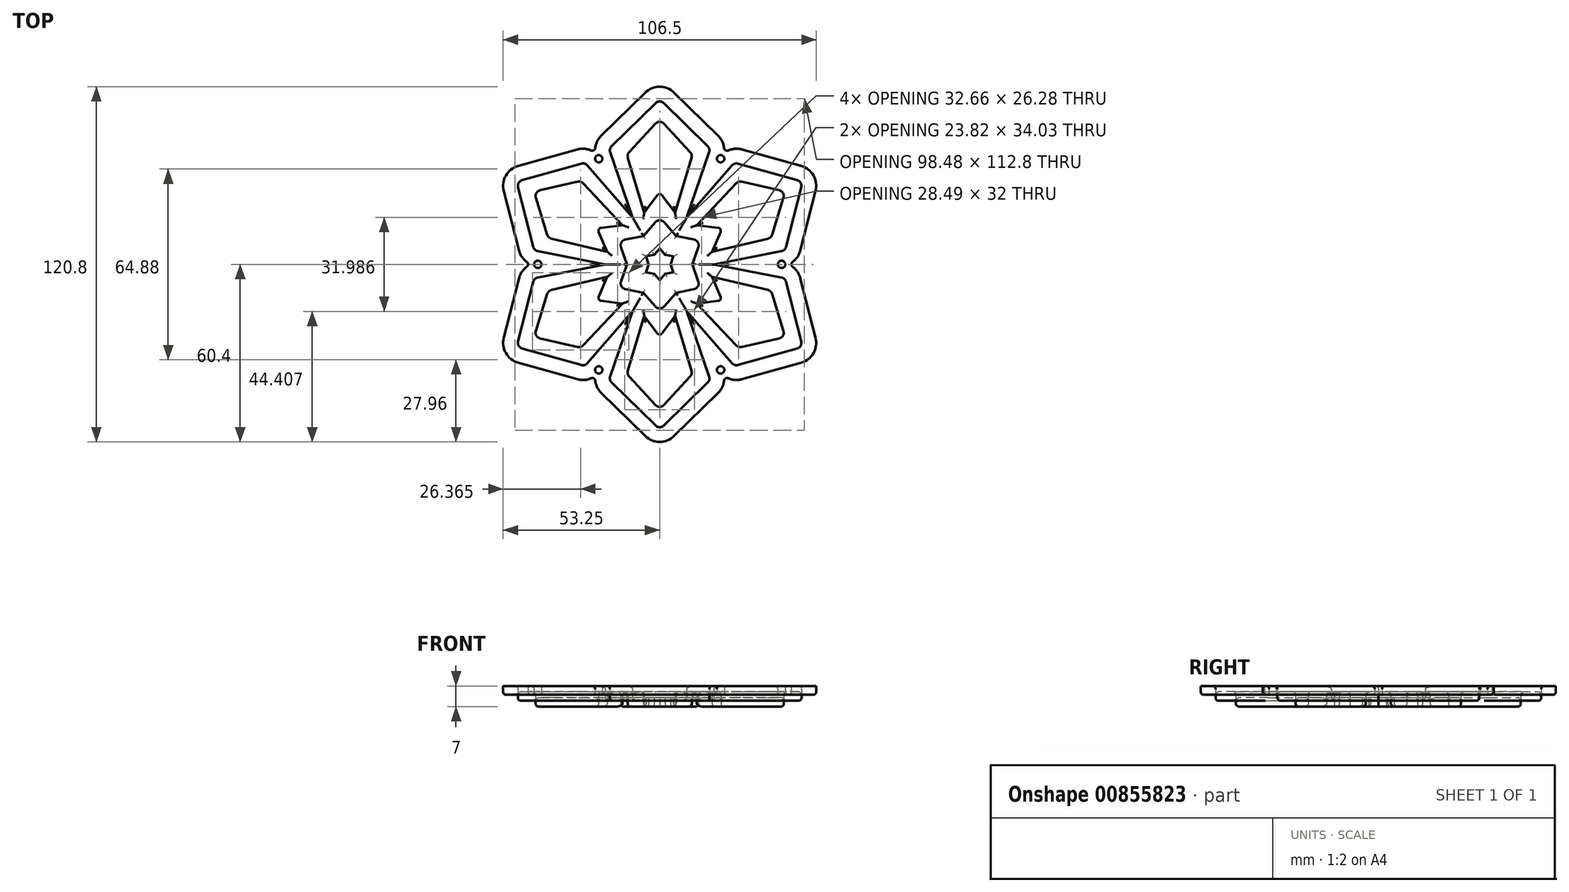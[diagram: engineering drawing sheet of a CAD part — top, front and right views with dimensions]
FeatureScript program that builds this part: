
annotation { "Feature Type Name" : "Feature", "Feature Type Description" : "" }
export const myFeature = defineFeature(function(context is Context, id is Id, definition is map)
    precondition{}
    {
        {
            var Q0;
            Q0=qCreatedBy(makeId("Top.planeOp"),FACE);
            var sketch = newSketch(context, id + "F0", { "sketchPlane" : qUnion([Q0])});
            skLineSegment(sketch, "E0", {"start": v(-3.74, 0) * mm, "end": v(-4.66, 2.7) * mm});
            skLineSegment(sketch, "E1", {"start": v(-16.34, 40.2) * mm, "end": v(-1.4, 54.83) * mm});
            skLineSegment(sketch, "E2.MirrorCS", {"start": v(16.34, 40.2) * mm, "end": v(1.4, 54.83) * mm});
            skLineSegment(sketch, "E3.MirrorCS", {"start": v(3.74, 0) * mm, "end": v(4.66, 2.7) * mm});
            skPoint(sketch, "E4.visualSharp", {"position": v(-17.25, 39.31) * mm});
            skArc(sketch, "E4.filletArc", {"start": v(-16.34, 40.2) * mm, "mid": v(-16.89, 39.23) * mm, "end": v(-16.83, 38.12) * mm});
            skPoint(sketch, "E5.visualSharp", {"position": v(17.25, 39.31) * mm});
            skArc(sketch, "E5.filletArc", {"start": v(16.83, 38.12) * mm, "mid": v(16.89, 39.23) * mm, "end": v(16.34, 40.2) * mm});
            skPoint(sketch, "E6.visualSharp", {"position": v(0, 56.2) * mm});
            skArc(sketch, "E6.filletArc", {"start": v(1.4, 54.83) * mm, "mid": v(0, 55.4) * mm, "end": v(-1.4, 54.83) * mm});
            skPoint(sketch, "E7.1.0", {"position": v(-48.67, 28.1) * mm});
            skPoint(sketch, "E7.1.1", {"position": v(-25.42, 34.6) * mm});
            skLineSegment(sketch, "E7.1.2", {"start": v(1.87, 3.24) * mm, "end": v(0, 5.38) * mm});
            skLineSegment(sketch, "E7.1.3", {"start": v(-26.64, 34.25) * mm, "end": v(-46.78, 28.63) * mm});
            skLineSegment(sketch, "E7.1.4", {"start": v(-42.98, 5.95) * mm, "end": v(-48.18, 26.2) * mm});
            skLineSegment(sketch, "E7.1.5", {"start": v(-1.87, -3.24) * mm, "end": v(-4.66, -2.7) * mm});
            skPoint(sketch, "E7.1.6", {"position": v(-42.67, 4.72) * mm});
            skArc(sketch, "E7.1.7", {"start": v(-46.78, 28.63) * mm, "mid": v(-47.98, 27.7) * mm, "end": v(-48.18, 26.2) * mm});
            skArc(sketch, "E7.1.8", {"start": v(-42.98, 5.95) * mm, "mid": v(-42.42, 4.99) * mm, "end": v(-41.43, 4.48) * mm});
            skArc(sketch, "E7.1.9", {"start": v(-24.6, 33.64) * mm, "mid": v(-25.53, 34.24) * mm, "end": v(-26.64, 34.25) * mm});
            skPoint(sketch, "E7.2.0", {"position": v(-48.67, -28.1) * mm});
            skPoint(sketch, "E7.2.1", {"position": v(-42.67, -4.72) * mm});
            skLineSegment(sketch, "E7.2.2", {"start": v(-1.87, 3.24) * mm, "end": v(-4.66, 2.7) * mm});
            skLineSegment(sketch, "E7.2.3", {"start": v(-42.98, -5.95) * mm, "end": v(-48.18, -26.2) * mm});
            skLineSegment(sketch, "E7.2.4", {"start": v(-26.64, -34.25) * mm, "end": v(-46.78, -28.63) * mm});
            skLineSegment(sketch, "E7.2.5", {"start": v(1.87, -3.24) * mm, "end": v(0, -5.38) * mm});
            skPoint(sketch, "E7.2.6", {"position": v(-25.42, -34.6) * mm});
            skArc(sketch, "E7.2.7", {"start": v(-48.18, -26.2) * mm, "mid": v(-47.98, -27.7) * mm, "end": v(-46.78, -28.63) * mm});
            skArc(sketch, "E7.2.8", {"start": v(-26.64, -34.25) * mm, "mid": v(-25.53, -34.24) * mm, "end": v(-24.6, -33.64) * mm});
            skArc(sketch, "E7.2.9", {"start": v(-41.43, -4.48) * mm, "mid": v(-42.42, -4.99) * mm, "end": v(-42.98, -5.95) * mm});
            skPoint(sketch, "E7.3.0", {"position": v(0, -56.2) * mm});
            skPoint(sketch, "E7.3.1", {"position": v(-17.25, -39.31) * mm});
            skLineSegment(sketch, "E7.3.2", {"start": v(-3.74, 0) * mm, "end": v(-4.66, -2.7) * mm});
            skLineSegment(sketch, "E7.3.3", {"start": v(-16.34, -40.2) * mm, "end": v(-1.4, -54.83) * mm});
            skLineSegment(sketch, "E7.3.4", {"start": v(16.34, -40.2) * mm, "end": v(1.4, -54.83) * mm});
            skLineSegment(sketch, "E7.3.5", {"start": v(3.74, 0) * mm, "end": v(4.66, -2.7) * mm});
            skPoint(sketch, "E7.3.6", {"position": v(17.25, -39.31) * mm});
            skArc(sketch, "E7.3.7", {"start": v(-1.4, -54.83) * mm, "mid": v(0, -55.4) * mm, "end": v(1.4, -54.83) * mm});
            skArc(sketch, "E7.3.8", {"start": v(16.34, -40.2) * mm, "mid": v(16.89, -39.23) * mm, "end": v(16.83, -38.12) * mm});
            skArc(sketch, "E7.3.9", {"start": v(-16.83, -38.12) * mm, "mid": v(-16.89, -39.23) * mm, "end": v(-16.34, -40.2) * mm});
            skPoint(sketch, "E7.4.0", {"position": v(48.67, -28.1) * mm});
            skPoint(sketch, "E7.4.1", {"position": v(25.42, -34.6) * mm});
            skLineSegment(sketch, "E7.4.2", {"start": v(-1.87, -3.24) * mm, "end": v(0, -5.38) * mm});
            skLineSegment(sketch, "E7.4.3", {"start": v(26.64, -34.25) * mm, "end": v(46.78, -28.63) * mm});
            skLineSegment(sketch, "E7.4.4", {"start": v(42.98, -5.95) * mm, "end": v(48.18, -26.2) * mm});
            skLineSegment(sketch, "E7.4.5", {"start": v(1.87, 3.24) * mm, "end": v(4.66, 2.7) * mm});
            skPoint(sketch, "E7.4.6", {"position": v(42.67, -4.72) * mm});
            skArc(sketch, "E7.4.7", {"start": v(46.78, -28.63) * mm, "mid": v(47.98, -27.7) * mm, "end": v(48.18, -26.2) * mm});
            skArc(sketch, "E7.4.8", {"start": v(42.98, -5.95) * mm, "mid": v(42.42, -4.99) * mm, "end": v(41.43, -4.48) * mm});
            skArc(sketch, "E7.4.9", {"start": v(24.6, -33.64) * mm, "mid": v(25.53, -34.24) * mm, "end": v(26.64, -34.25) * mm});
            skPoint(sketch, "E7.5.0", {"position": v(48.67, 28.1) * mm});
            skPoint(sketch, "E7.5.1", {"position": v(42.67, 4.72) * mm});
            skLineSegment(sketch, "E7.5.2", {"start": v(1.87, -3.24) * mm, "end": v(4.66, -2.7) * mm});
            skLineSegment(sketch, "E7.5.3", {"start": v(42.98, 5.95) * mm, "end": v(48.18, 26.2) * mm});
            skLineSegment(sketch, "E7.5.4", {"start": v(26.64, 34.25) * mm, "end": v(46.78, 28.63) * mm});
            skLineSegment(sketch, "E7.5.5", {"start": v(-1.87, 3.24) * mm, "end": v(0, 5.38) * mm});
            skPoint(sketch, "E7.5.6", {"position": v(25.42, 34.6) * mm});
            skArc(sketch, "E7.5.7", {"start": v(48.18, 26.2) * mm, "mid": v(47.98, 27.7) * mm, "end": v(46.78, 28.63) * mm});
            skArc(sketch, "E7.5.8", {"start": v(26.64, 34.25) * mm, "mid": v(25.53, 34.24) * mm, "end": v(24.6, 33.64) * mm});
            skArc(sketch, "E7.5.9", {"start": v(41.43, 4.48) * mm, "mid": v(42.42, 4.99) * mm, "end": v(42.98, 5.95) * mm});
            skPoint(sketch, "E7.center", {"position": v(0, 0) * mm});
            skLineSegment(sketch, "E8.trimOffspring", {"start": v(-9.23, 16) * mm, "end": v(-24.6, 33.64) * mm});
            skLineSegment(sketch, "E9.trimOffspring", {"start": v(-9.23, 16) * mm, "end": v(-16.83, 38.12) * mm});
            skLineSegment(sketch, "E10.trimOffspring", {"start": v(-18.46, 0) * mm, "end": v(-41.43, -4.48) * mm});
            skLineSegment(sketch, "E11.trimOffspring", {"start": v(-18.46, 0) * mm, "end": v(-41.43, 4.48) * mm});
            skLineSegment(sketch, "E12.trimOffspring", {"start": v(-9.23, -16) * mm, "end": v(-16.83, -38.12) * mm});
            skLineSegment(sketch, "E13.trimOffspring", {"start": v(-9.23, -16) * mm, "end": v(-24.6, -33.64) * mm});
            skLineSegment(sketch, "E14.trimOffspring", {"start": v(9.23, -16) * mm, "end": v(24.6, -33.64) * mm});
            skLineSegment(sketch, "E15.trimOffspring", {"start": v(9.23, -16) * mm, "end": v(16.83, -38.12) * mm});
            skLineSegment(sketch, "E16.trimOffspring", {"start": v(18.46, 0) * mm, "end": v(41.43, 4.48) * mm});
            skLineSegment(sketch, "E17.trimOffspring", {"start": v(18.46, 0) * mm, "end": v(41.43, -4.48) * mm});
            skLineSegment(sketch, "E18.trimOffspring", {"start": v(9.23, 16) * mm, "end": v(16.83, 38.12) * mm});
            skLineSegment(sketch, "E19.trimOffspring", {"start": v(9.23, 16) * mm, "end": v(24.6, 33.64) * mm});
            skLineSegment(sketch, "E20.0", {"start": v(-5.57, 9.65) * mm, "end": v(-11.64, 8.46) * mm});
            skLineSegment(sketch, "E20.1", {"start": v(11.14, 0) * mm, "end": v(13.15, -5.85) * mm});
            skLineSegment(sketch, "E20.2", {"start": v(11.14, 0) * mm, "end": v(13.15, 5.85) * mm});
            skLineSegment(sketch, "E20.3", {"start": v(5.57, 9.65) * mm, "end": v(11.64, 8.46) * mm});
            skLineSegment(sketch, "E20.4", {"start": v(5.57, 9.65) * mm, "end": v(1.5, 14.31) * mm});
            skLineSegment(sketch, "E20.5", {"start": v(5.57, -9.65) * mm, "end": v(11.64, -8.46) * mm});
            skLineSegment(sketch, "E20.6", {"start": v(-5.57, 9.65) * mm, "end": v(-1.5, 14.31) * mm});
            skLineSegment(sketch, "E20.7", {"start": v(5.57, -9.65) * mm, "end": v(1.5, -14.31) * mm});
            skLineSegment(sketch, "E20.8", {"start": v(-5.57, -9.65) * mm, "end": v(-1.5, -14.31) * mm});
            skLineSegment(sketch, "E20.9", {"start": v(-5.57, -9.65) * mm, "end": v(-11.64, -8.46) * mm});
            skLineSegment(sketch, "E20.10", {"start": v(-11.14, 0) * mm, "end": v(-13.15, -5.85) * mm});
            skLineSegment(sketch, "E20.11", {"start": v(-11.14, 0) * mm, "end": v(-13.15, 5.85) * mm});
            skLineSegment(sketch, "E21.0", {"start": v(-27.99, 39.07) * mm, "end": v(-48.13, 33.44) * mm});
            skLineSegment(sketch, "E22.0", {"start": v(-47.83, 4.7) * mm, "end": v(-53.03, 24.96) * mm});
            skArc(sketch, "E23.0", {"start": v(-48.13, 33.44) * mm, "mid": v(-52.3, 30.2) * mm, "end": v(-53.03, 24.96) * mm});
            skArc(sketch, "E24.0", {"start": v(-23.3, 38.74) * mm, "mid": v(-25.61, 39.3) * mm, "end": v(-27.99, 39.07) * mm});
            skArc(sketch, "E25.0", {"start": v(-47.83, 4.7) * mm, "mid": v(-46.85, 2.53) * mm, "end": v(-45.2, 0.8) * mm});
            skArc(sketch, "E26.1.1", {"start": v(-27.99, -39.07) * mm, "mid": v(-25.61, -39.3) * mm, "end": v(-23.3, -38.74) * mm});
            skLineSegment(sketch, "E26.1.2", {"start": v(-27.99, -39.07) * mm, "end": v(-48.13, -33.44) * mm});
            skArc(sketch, "E26.1.3", {"start": v(-53.03, -24.96) * mm, "mid": v(-52.3, -30.2) * mm, "end": v(-48.13, -33.44) * mm});
            skLineSegment(sketch, "E26.1.4", {"start": v(-47.83, -4.7) * mm, "end": v(-53.03, -24.96) * mm});
            skArc(sketch, "E26.1.5", {"start": v(-45.2, -0.8) * mm, "mid": v(-46.85, -2.53) * mm, "end": v(-47.83, -4.7) * mm});
            skArc(sketch, "E26.2.1", {"start": v(19.84, -43.77) * mm, "mid": v(21.24, -41.84) * mm, "end": v(21.9, -39.54) * mm});
            skLineSegment(sketch, "E26.2.2", {"start": v(19.84, -43.77) * mm, "end": v(4.9, -58.4) * mm});
            skArc(sketch, "E26.2.3", {"start": v(-4.9, -58.4) * mm, "mid": v(0, -60.4) * mm, "end": v(4.9, -58.4) * mm});
            skLineSegment(sketch, "E26.2.4", {"start": v(-19.84, -43.77) * mm, "end": v(-4.9, -58.4) * mm});
            skArc(sketch, "E26.2.5", {"start": v(-21.9, -39.54) * mm, "mid": v(-21.24, -41.84) * mm, "end": v(-19.84, -43.77) * mm});
            skArc(sketch, "E26.3.1", {"start": v(47.83, -4.7) * mm, "mid": v(46.85, -2.53) * mm, "end": v(45.2, -0.8) * mm});
            skLineSegment(sketch, "E26.3.2", {"start": v(47.83, -4.7) * mm, "end": v(53.03, -24.96) * mm});
            skArc(sketch, "E26.3.3", {"start": v(48.13, -33.44) * mm, "mid": v(52.3, -30.2) * mm, "end": v(53.03, -24.96) * mm});
            skLineSegment(sketch, "E26.3.4", {"start": v(27.99, -39.07) * mm, "end": v(48.13, -33.44) * mm});
            skArc(sketch, "E26.3.5", {"start": v(23.3, -38.74) * mm, "mid": v(25.61, -39.3) * mm, "end": v(27.99, -39.07) * mm});
            skArc(sketch, "E26.4.1", {"start": v(27.99, 39.07) * mm, "mid": v(25.61, 39.3) * mm, "end": v(23.3, 38.74) * mm});
            skLineSegment(sketch, "E26.4.2", {"start": v(27.99, 39.07) * mm, "end": v(48.13, 33.44) * mm});
            skArc(sketch, "E26.4.3", {"start": v(53.03, 24.96) * mm, "mid": v(52.3, 30.2) * mm, "end": v(48.13, 33.44) * mm});
            skLineSegment(sketch, "E26.4.4", {"start": v(47.83, 4.7) * mm, "end": v(53.03, 24.96) * mm});
            skArc(sketch, "E26.4.5", {"start": v(45.2, 0.8) * mm, "mid": v(46.85, 2.53) * mm, "end": v(47.83, 4.7) * mm});
            skArc(sketch, "E26.5.1", {"start": v(-19.84, 43.77) * mm, "mid": v(-21.24, 41.84) * mm, "end": v(-21.9, 39.54) * mm});
            skLineSegment(sketch, "E26.5.2", {"start": v(-19.84, 43.77) * mm, "end": v(-4.9, 58.4) * mm});
            skArc(sketch, "E26.5.3", {"start": v(4.9, 58.4) * mm, "mid": v(0, 60.4) * mm, "end": v(-4.9, 58.4) * mm});
            skLineSegment(sketch, "E26.5.4", {"start": v(19.84, 43.77) * mm, "end": v(4.9, 58.4) * mm});
            skArc(sketch, "E26.5.5", {"start": v(21.9, 39.54) * mm, "mid": v(21.24, 41.84) * mm, "end": v(19.84, 43.77) * mm});
            skPoint(sketch, "E27.orphan", {"position": v(-20.82, 36.92) * mm});
            skPoint(sketch, "E28.orphan", {"position": v(-21.56, 36.5) * mm});
            skPoint(sketch, "E29.orphan", {"position": v(20.82, 36.92) * mm});
            skPoint(sketch, "E30.orphan", {"position": v(21.56, 36.5) * mm});
            skPoint(sketch, "E31.orphan", {"position": v(42.39, 0.43) * mm});
            skPoint(sketch, "E32.orphan", {"position": v(42.39, -0.43) * mm});
            skPoint(sketch, "E33.orphan", {"position": v(21.56, -36.5) * mm});
            skPoint(sketch, "E34.orphan", {"position": v(20.82, -36.92) * mm});
            skPoint(sketch, "E35.orphan", {"position": v(-20.82, -36.92) * mm});
            skPoint(sketch, "E36.orphan", {"position": v(-21.56, -36.5) * mm});
            skPoint(sketch, "E37.orphan", {"position": v(-42.39, 0.43) * mm});
            skPoint(sketch, "E38.orphan", {"position": v(-42.39, -0.43) * mm});
            skLineSegment(sketch, "E39", {"start": v(-0.8, 23.48) * mm, "end": v(-5.22, 17.6) * mm});
            skLineSegment(sketch, "E40", {"start": v(-5.22, 17.6) * mm, "end": v(-10.83, 36.26) * mm});
            skLineSegment(sketch, "E41", {"start": v(-10.38, 38.2) * mm, "end": v(-1.47, 47.81) * mm});
            skLineSegment(sketch, "E42.MirrorCS", {"start": v(10.38, 38.2) * mm, "end": v(1.47, 47.81) * mm});
            skLineSegment(sketch, "E43.MirrorCS", {"start": v(5.22, 17.6) * mm, "end": v(10.83, 36.26) * mm});
            skLineSegment(sketch, "E44.MirrorCS", {"start": v(0.8, 23.48) * mm, "end": v(5.22, 17.6) * mm});
            skPoint(sketch, "E45.visualSharp", {"position": v(0, 49.4) * mm});
            skArc(sketch, "E45.filletArc", {"start": v(1.47, 47.81) * mm, "mid": v(0, 48.45) * mm, "end": v(-1.47, 47.81) * mm});
            skPoint(sketch, "E46.visualSharp", {"position": v(-11.16, 37.35) * mm});
            skArc(sketch, "E46.filletArc", {"start": v(-10.38, 38.2) * mm, "mid": v(-10.86, 37.28) * mm, "end": v(-10.83, 36.26) * mm});
            skPoint(sketch, "E47.visualSharp", {"position": v(11.16, 37.35) * mm});
            skArc(sketch, "E47.filletArc", {"start": v(10.83, 36.26) * mm, "mid": v(10.86, 37.28) * mm, "end": v(10.38, 38.2) * mm});
            skPoint(sketch, "E48.visualSharp", {"position": v(0, 24.54) * mm});
            skArc(sketch, "E48.filletArc", {"start": v(0.8, 23.48) * mm, "mid": v(0, 23.88) * mm, "end": v(-0.8, 23.48) * mm});
            skPoint(sketch, "E49.visualSharp", {"position": v(0, 16.05) * mm});
            skArc(sketch, "E49.filletArc", {"start": v(1.5, 14.31) * mm, "mid": v(0, 15) * mm, "end": v(-1.5, 14.31) * mm});
            skPoint(sketch, "E50.visualSharp", {"position": v(13.9, 8.02) * mm});
            skArc(sketch, "E50.filletArc", {"start": v(13.15, 5.85) * mm, "mid": v(13, 7.5) * mm, "end": v(11.64, 8.46) * mm});
            skPoint(sketch, "E51.visualSharp", {"position": v(13.9, -8.02) * mm});
            skArc(sketch, "E51.filletArc", {"start": v(11.64, -8.46) * mm, "mid": v(13, -7.5) * mm, "end": v(13.15, -5.85) * mm});
            skPoint(sketch, "E52.visualSharp", {"position": v(0, -16.05) * mm});
            skArc(sketch, "E52.filletArc", {"start": v(-1.5, -14.31) * mm, "mid": v(0, -15) * mm, "end": v(1.5, -14.31) * mm});
            skPoint(sketch, "E53.visualSharp", {"position": v(-13.9, -8.02) * mm});
            skArc(sketch, "E53.filletArc", {"start": v(-13.15, -5.85) * mm, "mid": v(-13, -7.5) * mm, "end": v(-11.64, -8.46) * mm});
            skPoint(sketch, "E54.visualSharp", {"position": v(-13.9, 8.02) * mm});
            skArc(sketch, "E54.filletArc", {"start": v(-11.64, 8.46) * mm, "mid": v(-13, 7.5) * mm, "end": v(-13.15, 5.85) * mm});
            skArc(sketch, "E55.1.0", {"start": v(-25.99, 27.5) * mm, "mid": v(-26.86, 28.05) * mm, "end": v(-27.89, 28.09) * mm});
            skLineSegment(sketch, "E55.1.1", {"start": v(-27.89, 28.09) * mm, "end": v(-40.67, 25.18) * mm});
            skArc(sketch, "E55.1.2", {"start": v(-40.67, 25.18) * mm, "mid": v(-41.96, 24.23) * mm, "end": v(-42.14, 22.64) * mm});
            skLineSegment(sketch, "E55.1.3", {"start": v(-38.27, 10.1) * mm, "end": v(-42.14, 22.64) * mm});
            skArc(sketch, "E55.1.4", {"start": v(-38.27, 10.1) * mm, "mid": v(-37.72, 9.24) * mm, "end": v(-36.81, 8.75) * mm});
            skLineSegment(sketch, "E55.1.5", {"start": v(-17.86, 4.28) * mm, "end": v(-36.81, 8.75) * mm});
            skLineSegment(sketch, "E55.1.6", {"start": v(-20.73, 11.05) * mm, "end": v(-17.86, 4.28) * mm});
            skArc(sketch, "E55.1.7", {"start": v(-19.93, 12.43) * mm, "mid": v(-20.68, 11.94) * mm, "end": v(-20.73, 11.05) * mm});
            skLineSegment(sketch, "E55.1.8", {"start": v(-19.93, 12.43) * mm, "end": v(-12.63, 13.33) * mm});
            skLineSegment(sketch, "E55.1.9", {"start": v(-12.63, 13.33) * mm, "end": v(-25.99, 27.5) * mm});
            skArc(sketch, "E55.2.0", {"start": v(-36.81, -8.75) * mm, "mid": v(-37.72, -9.24) * mm, "end": v(-38.27, -10.1) * mm});
            skLineSegment(sketch, "E55.2.1", {"start": v(-38.27, -10.1) * mm, "end": v(-42.14, -22.64) * mm});
            skArc(sketch, "E55.2.2", {"start": v(-42.14, -22.64) * mm, "mid": v(-41.96, -24.23) * mm, "end": v(-40.67, -25.18) * mm});
            skLineSegment(sketch, "E55.2.3", {"start": v(-27.89, -28.09) * mm, "end": v(-40.67, -25.18) * mm});
            skArc(sketch, "E55.2.4", {"start": v(-27.89, -28.09) * mm, "mid": v(-26.86, -28.05) * mm, "end": v(-25.99, -27.5) * mm});
            skLineSegment(sketch, "E55.2.5", {"start": v(-12.63, -13.33) * mm, "end": v(-25.99, -27.5) * mm});
            skLineSegment(sketch, "E55.2.6", {"start": v(-19.93, -12.43) * mm, "end": v(-12.63, -13.33) * mm});
            skArc(sketch, "E55.2.7", {"start": v(-20.73, -11.05) * mm, "mid": v(-20.68, -11.94) * mm, "end": v(-19.93, -12.43) * mm});
            skLineSegment(sketch, "E55.2.8", {"start": v(-20.73, -11.05) * mm, "end": v(-17.86, -4.28) * mm});
            skLineSegment(sketch, "E55.2.9", {"start": v(-17.86, -4.28) * mm, "end": v(-36.81, -8.75) * mm});
            skArc(sketch, "E56.1.3.0", {"start": v(-10.83, -36.26) * mm, "mid": v(-10.86, -37.28) * mm, "end": v(-10.38, -38.2) * mm});
            skLineSegment(sketch, "E56.4.3.0", {"start": v(-10.38, -38.2) * mm, "end": v(-1.47, -47.81) * mm});
            skArc(sketch, "E56.7.3.0", {"start": v(-1.47, -47.81) * mm, "mid": v(0, -48.45) * mm, "end": v(1.47, -47.81) * mm});
            skLineSegment(sketch, "E56.11.3.0", {"start": v(10.38, -38.2) * mm, "end": v(1.47, -47.81) * mm});
            skArc(sketch, "E56.14.3.0", {"start": v(10.38, -38.2) * mm, "mid": v(10.86, -37.28) * mm, "end": v(10.83, -36.26) * mm});
            skLineSegment(sketch, "E56.18.3.0", {"start": v(5.22, -17.6) * mm, "end": v(10.83, -36.26) * mm});
            skLineSegment(sketch, "E56.21.3.0", {"start": v(0.8, -23.48) * mm, "end": v(5.22, -17.6) * mm});
            skArc(sketch, "E56.24.3.0", {"start": v(-0.8, -23.48) * mm, "mid": v(0, -23.88) * mm, "end": v(0.8, -23.48) * mm});
            skLineSegment(sketch, "E56.28.3.0", {"start": v(-0.8, -23.48) * mm, "end": v(-5.22, -17.6) * mm});
            skLineSegment(sketch, "E56.31.3.0", {"start": v(-5.22, -17.6) * mm, "end": v(-10.83, -36.26) * mm});
            skArc(sketch, "E56.1.4.0", {"start": v(25.99, -27.5) * mm, "mid": v(26.86, -28.05) * mm, "end": v(27.89, -28.09) * mm});
            skLineSegment(sketch, "E56.4.4.0", {"start": v(27.89, -28.09) * mm, "end": v(40.67, -25.18) * mm});
            skArc(sketch, "E56.7.4.0", {"start": v(40.67, -25.18) * mm, "mid": v(41.96, -24.23) * mm, "end": v(42.14, -22.64) * mm});
            skLineSegment(sketch, "E56.11.4.0", {"start": v(38.27, -10.1) * mm, "end": v(42.14, -22.64) * mm});
            skArc(sketch, "E56.14.4.0", {"start": v(38.27, -10.1) * mm, "mid": v(37.72, -9.24) * mm, "end": v(36.81, -8.75) * mm});
            skLineSegment(sketch, "E56.18.4.0", {"start": v(17.86, -4.28) * mm, "end": v(36.81, -8.75) * mm});
            skLineSegment(sketch, "E56.21.4.0", {"start": v(20.73, -11.05) * mm, "end": v(17.86, -4.28) * mm});
            skArc(sketch, "E56.24.4.0", {"start": v(19.93, -12.43) * mm, "mid": v(20.68, -11.94) * mm, "end": v(20.73, -11.05) * mm});
            skLineSegment(sketch, "E56.28.4.0", {"start": v(19.93, -12.43) * mm, "end": v(12.63, -13.33) * mm});
            skLineSegment(sketch, "E56.31.4.0", {"start": v(12.63, -13.33) * mm, "end": v(25.99, -27.5) * mm});
            skArc(sketch, "E56.1.5.0", {"start": v(36.81, 8.75) * mm, "mid": v(37.72, 9.24) * mm, "end": v(38.27, 10.1) * mm});
            skLineSegment(sketch, "E56.4.5.0", {"start": v(38.27, 10.1) * mm, "end": v(42.14, 22.64) * mm});
            skArc(sketch, "E56.7.5.0", {"start": v(42.14, 22.64) * mm, "mid": v(41.96, 24.23) * mm, "end": v(40.67, 25.18) * mm});
            skLineSegment(sketch, "E56.11.5.0", {"start": v(27.89, 28.09) * mm, "end": v(40.67, 25.18) * mm});
            skArc(sketch, "E56.14.5.0", {"start": v(27.89, 28.09) * mm, "mid": v(26.86, 28.05) * mm, "end": v(25.99, 27.5) * mm});
            skLineSegment(sketch, "E56.18.5.0", {"start": v(12.63, 13.33) * mm, "end": v(25.99, 27.5) * mm});
            skLineSegment(sketch, "E56.21.5.0", {"start": v(19.93, 12.43) * mm, "end": v(12.63, 13.33) * mm});
            skArc(sketch, "E56.24.5.0", {"start": v(20.73, 11.05) * mm, "mid": v(20.68, 11.94) * mm, "end": v(19.93, 12.43) * mm});
            skLineSegment(sketch, "E56.28.5.0", {"start": v(20.73, 11.05) * mm, "end": v(17.86, 4.28) * mm});
            skLineSegment(sketch, "E56.31.5.0", {"start": v(17.86, 4.28) * mm, "end": v(36.81, 8.75) * mm});
            skCircle(sketch, "E57", {"center": v(-41.46, 0) * mm, "radius": 1.25 * mm});
            skCircle(sketch, "E58.1.0", {"center": v(-20.73, -35.9) * mm, "radius": 1.25 * mm});
            skCircle(sketch, "E58.2.0", {"center": v(20.73, -35.9) * mm, "radius": 1.25 * mm});
            skCircle(sketch, "E58.3.0", {"center": v(41.46, 0) * mm, "radius": 1.25 * mm});
            skCircle(sketch, "E58.4.0", {"center": v(20.73, 35.9) * mm, "radius": 1.25 * mm});
            skCircle(sketch, "E58.5.0", {"center": v(-20.73, 35.9) * mm, "radius": 1.25 * mm});
            skPoint(sketch, "E59.visualSharp", {"position": v(21.9, 37.92) * mm});
            skArc(sketch, "E59.filletArc", {"start": v(21.9, 39.54) * mm, "mid": v(22.4, 38.79) * mm, "end": v(23.3, 38.74) * mm});
            skPoint(sketch, "E60.visualSharp", {"position": v(43.78, 0) * mm});
            skArc(sketch, "E60.filletArc", {"start": v(45.2, 0.8) * mm, "mid": v(44.79, 0) * mm, "end": v(45.2, -0.8) * mm});
            skPoint(sketch, "E61.visualSharp", {"position": v(21.9, -37.92) * mm});
            skArc(sketch, "E61.filletArc", {"start": v(23.3, -38.74) * mm, "mid": v(22.4, -38.79) * mm, "end": v(21.9, -39.54) * mm});
            skPoint(sketch, "E62.visualSharp", {"position": v(-21.9, -37.92) * mm});
            skArc(sketch, "E62.filletArc", {"start": v(-21.9, -39.54) * mm, "mid": v(-22.4, -38.79) * mm, "end": v(-23.3, -38.74) * mm});
            skPoint(sketch, "E63.visualSharp", {"position": v(-43.78, 0) * mm});
            skArc(sketch, "E63.filletArc", {"start": v(-45.2, -0.8) * mm, "mid": v(-44.79, 0) * mm, "end": v(-45.2, 0.8) * mm});
            skPoint(sketch, "E64.visualSharp", {"position": v(-21.9, 37.92) * mm});
            skArc(sketch, "E64.filletArc", {"start": v(-23.3, 38.74) * mm, "mid": v(-22.4, 38.79) * mm, "end": v(-21.9, 39.54) * mm});
            skSolve(sketch);
        }
        {
            var Q0;
            Q0=qCreatedBy(makeId("Top.planeOp"),FACE);
            cPlane(context, id + "F1", {"entities" : qUnion([Q0]), "cplaneType" : CPlaneType.OFFSET, "offset" : 2 * mm, "oppositeDirection" : true, "width" : 150 * mm, "height" : 150 * mm});
        }
        {
            var Q0;
            Q0=qCreatedBy(id+"F1.planeOp",FACE);
            var sketch = newSketch(context, id + "F2", { "sketchPlane" : qUnion([Q0])});
            skLineSegment(sketch, "E65.0.0", {"start": v(-9.23, -16) * mm, "end": v(-16.83, -38.12) * mm});
            skArc(sketch, "E65.0.1", {"start": v(-16.83, -38.12) * mm, "mid": v(-16.89, -39.23) * mm, "end": v(-16.34, -40.2) * mm});
            skLineSegment(sketch, "E65.0.2", {"start": v(-16.34, -40.2) * mm, "end": v(-1.4, -54.83) * mm});
            skArc(sketch, "E65.0.3", {"start": v(-1.4, -54.83) * mm, "mid": v(0, -55.4) * mm, "end": v(1.4, -54.83) * mm});
            skLineSegment(sketch, "E65.0.4", {"start": v(1.4, -54.83) * mm, "end": v(16.34, -40.2) * mm});
            skArc(sketch, "E65.0.5", {"start": v(16.34, -40.2) * mm, "mid": v(16.89, -39.23) * mm, "end": v(16.83, -38.12) * mm});
            skLineSegment(sketch, "E65.0.6", {"start": v(16.83, -38.12) * mm, "end": v(9.23, -16) * mm});
            skLineSegment(sketch, "E65.0.7", {"start": v(9.23, -16) * mm, "end": v(24.6, -33.64) * mm});
            skArc(sketch, "E65.0.8", {"start": v(24.6, -33.64) * mm, "mid": v(25.53, -34.24) * mm, "end": v(26.64, -34.25) * mm});
            skLineSegment(sketch, "E65.0.9", {"start": v(26.64, -34.25) * mm, "end": v(46.78, -28.63) * mm});
            skArc(sketch, "E65.0.10", {"start": v(46.78, -28.63) * mm, "mid": v(47.98, -27.7) * mm, "end": v(48.18, -26.2) * mm});
            skLineSegment(sketch, "E65.0.11", {"start": v(48.18, -26.2) * mm, "end": v(42.98, -5.95) * mm});
            skArc(sketch, "E65.0.12", {"start": v(42.98, -5.95) * mm, "mid": v(42.42, -4.99) * mm, "end": v(41.43, -4.48) * mm});
            skLineSegment(sketch, "E65.0.13", {"start": v(41.43, -4.48) * mm, "end": v(18.46, 0) * mm});
            skLineSegment(sketch, "E65.0.14", {"start": v(18.46, 0) * mm, "end": v(41.43, 4.48) * mm});
            skArc(sketch, "E65.0.15", {"start": v(41.43, 4.48) * mm, "mid": v(42.42, 4.99) * mm, "end": v(42.98, 5.95) * mm});
            skLineSegment(sketch, "E65.0.16", {"start": v(42.98, 5.95) * mm, "end": v(48.18, 26.2) * mm});
            skArc(sketch, "E65.0.17", {"start": v(48.18, 26.2) * mm, "mid": v(47.98, 27.7) * mm, "end": v(46.78, 28.63) * mm});
            skLineSegment(sketch, "E65.0.18", {"start": v(46.78, 28.63) * mm, "end": v(26.64, 34.25) * mm});
            skArc(sketch, "E65.0.19", {"start": v(26.64, 34.25) * mm, "mid": v(25.53, 34.24) * mm, "end": v(24.6, 33.64) * mm});
            skLineSegment(sketch, "E65.0.20", {"start": v(24.6, 33.64) * mm, "end": v(9.23, 16) * mm});
            skLineSegment(sketch, "E65.0.21", {"start": v(9.23, 16) * mm, "end": v(16.83, 38.12) * mm});
            skArc(sketch, "E65.0.22", {"start": v(16.83, 38.12) * mm, "mid": v(16.89, 39.23) * mm, "end": v(16.34, 40.2) * mm});
            skLineSegment(sketch, "E65.0.23", {"start": v(16.34, 40.2) * mm, "end": v(1.4, 54.83) * mm});
            skArc(sketch, "E65.0.24", {"start": v(1.4, 54.83) * mm, "mid": v(0, 55.4) * mm, "end": v(-1.4, 54.83) * mm});
            skLineSegment(sketch, "E65.0.25", {"start": v(-1.4, 54.83) * mm, "end": v(-16.34, 40.2) * mm});
            skArc(sketch, "E65.0.26", {"start": v(-16.34, 40.2) * mm, "mid": v(-16.89, 39.23) * mm, "end": v(-16.83, 38.12) * mm});
            skLineSegment(sketch, "E65.0.27", {"start": v(-16.83, 38.12) * mm, "end": v(-9.23, 16) * mm});
            skLineSegment(sketch, "E65.0.28", {"start": v(-9.23, 16) * mm, "end": v(-24.6, 33.64) * mm});
            skArc(sketch, "E65.0.29", {"start": v(-24.6, 33.64) * mm, "mid": v(-25.53, 34.24) * mm, "end": v(-26.64, 34.25) * mm});
            skLineSegment(sketch, "E65.0.30", {"start": v(-26.64, 34.25) * mm, "end": v(-46.78, 28.63) * mm});
            skArc(sketch, "E65.0.31", {"start": v(-46.78, 28.63) * mm, "mid": v(-47.98, 27.7) * mm, "end": v(-48.18, 26.2) * mm});
            skLineSegment(sketch, "E65.0.32", {"start": v(-48.18, 26.2) * mm, "end": v(-42.98, 5.95) * mm});
            skArc(sketch, "E65.0.33", {"start": v(-42.98, 5.95) * mm, "mid": v(-42.42, 4.99) * mm, "end": v(-41.43, 4.48) * mm});
            skLineSegment(sketch, "E65.0.34", {"start": v(-41.43, 4.48) * mm, "end": v(-18.46, 0) * mm});
            skLineSegment(sketch, "E65.0.35", {"start": v(-18.46, 0) * mm, "end": v(-41.43, -4.48) * mm});
            skArc(sketch, "E65.0.36", {"start": v(-41.43, -4.48) * mm, "mid": v(-42.42, -4.99) * mm, "end": v(-42.98, -5.95) * mm});
            skLineSegment(sketch, "E65.0.37", {"start": v(-42.98, -5.95) * mm, "end": v(-48.18, -26.2) * mm});
            skArc(sketch, "E65.0.38", {"start": v(-48.18, -26.2) * mm, "mid": v(-47.98, -27.7) * mm, "end": v(-46.78, -28.63) * mm});
            skLineSegment(sketch, "E65.0.39", {"start": v(-46.78, -28.63) * mm, "end": v(-26.64, -34.25) * mm});
            skArc(sketch, "E65.0.40", {"start": v(-26.64, -34.25) * mm, "mid": v(-25.53, -34.24) * mm, "end": v(-24.6, -33.64) * mm});
            skLineSegment(sketch, "E65.0.41", {"start": v(-24.6, -33.64) * mm, "end": v(-9.23, -16) * mm});
            skLineSegment(sketch, "E66.0.0", {"start": v(19.93, -12.43) * mm, "end": v(12.63, -13.33) * mm});
            skLineSegment(sketch, "E66.0.1", {"start": v(12.63, -13.33) * mm, "end": v(25.99, -27.5) * mm});
            skArc(sketch, "E66.0.2", {"start": v(25.99, -27.5) * mm, "mid": v(26.86, -28.05) * mm, "end": v(27.89, -28.09) * mm});
            skLineSegment(sketch, "E66.0.3", {"start": v(27.89, -28.09) * mm, "end": v(40.67, -25.18) * mm});
            skArc(sketch, "E66.0.4", {"start": v(40.67, -25.18) * mm, "mid": v(41.96, -24.23) * mm, "end": v(42.14, -22.64) * mm});
            skLineSegment(sketch, "E66.0.5", {"start": v(42.14, -22.64) * mm, "end": v(38.27, -10.1) * mm});
            skArc(sketch, "E66.0.6", {"start": v(38.27, -10.1) * mm, "mid": v(37.72, -9.24) * mm, "end": v(36.81, -8.75) * mm});
            skLineSegment(sketch, "E66.0.7", {"start": v(36.81, -8.75) * mm, "end": v(17.86, -4.28) * mm});
            skLineSegment(sketch, "E66.0.8", {"start": v(17.86, -4.28) * mm, "end": v(20.73, -11.05) * mm});
            skArc(sketch, "E66.0.9", {"start": v(20.73, -11.05) * mm, "mid": v(20.68, -11.94) * mm, "end": v(19.93, -12.43) * mm});
            skLineSegment(sketch, "E67.0.0", {"start": v(-0.8, -23.48) * mm, "end": v(-5.22, -17.6) * mm});
            skLineSegment(sketch, "E67.0.1", {"start": v(-5.22, -17.6) * mm, "end": v(-10.83, -36.26) * mm});
            skArc(sketch, "E67.0.2", {"start": v(-10.83, -36.26) * mm, "mid": v(-10.86, -37.28) * mm, "end": v(-10.38, -38.2) * mm});
            skLineSegment(sketch, "E67.0.3", {"start": v(-10.38, -38.2) * mm, "end": v(-1.47, -47.81) * mm});
            skArc(sketch, "E67.0.4", {"start": v(-1.47, -47.81) * mm, "mid": v(0, -48.45) * mm, "end": v(1.47, -47.81) * mm});
            skLineSegment(sketch, "E67.0.5", {"start": v(1.47, -47.81) * mm, "end": v(10.38, -38.2) * mm});
            skArc(sketch, "E67.0.6", {"start": v(10.38, -38.2) * mm, "mid": v(10.86, -37.28) * mm, "end": v(10.83, -36.26) * mm});
            skLineSegment(sketch, "E67.0.7", {"start": v(10.83, -36.26) * mm, "end": v(5.22, -17.6) * mm});
            skLineSegment(sketch, "E67.0.8", {"start": v(5.22, -17.6) * mm, "end": v(0.8, -23.48) * mm});
            skArc(sketch, "E67.0.9", {"start": v(0.8, -23.48) * mm, "mid": v(0, -23.88) * mm, "end": v(-0.8, -23.48) * mm});
            skLineSegment(sketch, "E68.0.0", {"start": v(-20.73, -11.05) * mm, "end": v(-17.86, -4.28) * mm});
            skLineSegment(sketch, "E68.0.1", {"start": v(-17.86, -4.28) * mm, "end": v(-36.81, -8.75) * mm});
            skArc(sketch, "E68.0.2", {"start": v(-36.81, -8.75) * mm, "mid": v(-37.72, -9.24) * mm, "end": v(-38.27, -10.1) * mm});
            skLineSegment(sketch, "E68.0.3", {"start": v(-38.27, -10.1) * mm, "end": v(-42.14, -22.64) * mm});
            skArc(sketch, "E68.0.4", {"start": v(-42.14, -22.64) * mm, "mid": v(-41.96, -24.23) * mm, "end": v(-40.67, -25.18) * mm});
            skLineSegment(sketch, "E68.0.5", {"start": v(-40.67, -25.18) * mm, "end": v(-27.89, -28.09) * mm});
            skArc(sketch, "E68.0.6", {"start": v(-27.89, -28.09) * mm, "mid": v(-26.86, -28.05) * mm, "end": v(-25.99, -27.5) * mm});
            skLineSegment(sketch, "E68.0.7", {"start": v(-25.99, -27.5) * mm, "end": v(-12.63, -13.33) * mm});
            skLineSegment(sketch, "E68.0.8", {"start": v(-12.63, -13.33) * mm, "end": v(-19.93, -12.43) * mm});
            skArc(sketch, "E68.0.9", {"start": v(-19.93, -12.43) * mm, "mid": v(-20.68, -11.94) * mm, "end": v(-20.73, -11.05) * mm});
            skLineSegment(sketch, "E69.0.0", {"start": v(-19.93, 12.43) * mm, "end": v(-12.63, 13.33) * mm});
            skLineSegment(sketch, "E69.0.1", {"start": v(-12.63, 13.33) * mm, "end": v(-25.99, 27.5) * mm});
            skArc(sketch, "E69.0.2", {"start": v(-25.99, 27.5) * mm, "mid": v(-26.86, 28.05) * mm, "end": v(-27.89, 28.09) * mm});
            skLineSegment(sketch, "E69.0.3", {"start": v(-27.89, 28.09) * mm, "end": v(-40.67, 25.18) * mm});
            skArc(sketch, "E69.0.4", {"start": v(-40.67, 25.18) * mm, "mid": v(-41.96, 24.23) * mm, "end": v(-42.14, 22.64) * mm});
            skLineSegment(sketch, "E69.0.5", {"start": v(-42.14, 22.64) * mm, "end": v(-38.27, 10.1) * mm});
            skArc(sketch, "E69.0.6", {"start": v(-38.27, 10.1) * mm, "mid": v(-37.72, 9.24) * mm, "end": v(-36.81, 8.75) * mm});
            skLineSegment(sketch, "E69.0.7", {"start": v(-36.81, 8.75) * mm, "end": v(-17.86, 4.28) * mm});
            skLineSegment(sketch, "E69.0.8", {"start": v(-17.86, 4.28) * mm, "end": v(-20.73, 11.05) * mm});
            skArc(sketch, "E69.0.9", {"start": v(-20.73, 11.05) * mm, "mid": v(-20.68, 11.94) * mm, "end": v(-19.93, 12.43) * mm});
            skLineSegment(sketch, "E70.0.0", {"start": v(5.22, 17.6) * mm, "end": v(10.83, 36.26) * mm});
            skArc(sketch, "E70.0.1", {"start": v(10.83, 36.26) * mm, "mid": v(10.86, 37.28) * mm, "end": v(10.38, 38.2) * mm});
            skLineSegment(sketch, "E70.0.2", {"start": v(10.38, 38.2) * mm, "end": v(1.47, 47.81) * mm});
            skArc(sketch, "E70.0.3", {"start": v(1.47, 47.81) * mm, "mid": v(0, 48.45) * mm, "end": v(-1.47, 47.81) * mm});
            skLineSegment(sketch, "E70.0.4", {"start": v(-1.47, 47.81) * mm, "end": v(-10.38, 38.2) * mm});
            skArc(sketch, "E70.0.5", {"start": v(-10.38, 38.2) * mm, "mid": v(-10.86, 37.28) * mm, "end": v(-10.83, 36.26) * mm});
            skLineSegment(sketch, "E70.0.6", {"start": v(-10.83, 36.26) * mm, "end": v(-5.22, 17.6) * mm});
            skLineSegment(sketch, "E70.0.7", {"start": v(-5.22, 17.6) * mm, "end": v(-0.8, 23.48) * mm});
            skArc(sketch, "E70.0.8", {"start": v(-0.8, 23.48) * mm, "mid": v(0, 23.88) * mm, "end": v(0.8, 23.48) * mm});
            skLineSegment(sketch, "E70.0.9", {"start": v(0.8, 23.48) * mm, "end": v(5.22, 17.6) * mm});
            skLineSegment(sketch, "E71.0.0", {"start": v(20.73, 11.05) * mm, "end": v(17.86, 4.28) * mm});
            skLineSegment(sketch, "E71.0.1", {"start": v(17.86, 4.28) * mm, "end": v(36.81, 8.75) * mm});
            skArc(sketch, "E71.0.2", {"start": v(36.81, 8.75) * mm, "mid": v(37.72, 9.24) * mm, "end": v(38.27, 10.1) * mm});
            skLineSegment(sketch, "E71.0.3", {"start": v(38.27, 10.1) * mm, "end": v(42.14, 22.64) * mm});
            skArc(sketch, "E71.0.4", {"start": v(42.14, 22.64) * mm, "mid": v(41.96, 24.23) * mm, "end": v(40.67, 25.18) * mm});
            skLineSegment(sketch, "E71.0.5", {"start": v(40.67, 25.18) * mm, "end": v(27.89, 28.09) * mm});
            skArc(sketch, "E71.0.6", {"start": v(27.89, 28.09) * mm, "mid": v(26.86, 28.05) * mm, "end": v(25.99, 27.5) * mm});
            skLineSegment(sketch, "E71.0.7", {"start": v(25.99, 27.5) * mm, "end": v(12.63, 13.33) * mm});
            skLineSegment(sketch, "E71.0.8", {"start": v(12.63, 13.33) * mm, "end": v(19.93, 12.43) * mm});
            skArc(sketch, "E71.0.9", {"start": v(19.93, 12.43) * mm, "mid": v(20.68, 11.94) * mm, "end": v(20.73, 11.05) * mm});
            skLineSegment(sketch, "E72.0.0", {"start": v(1.5, -14.31) * mm, "end": v(5.57, -9.65) * mm});
            skLineSegment(sketch, "E72.0.1", {"start": v(5.57, -9.65) * mm, "end": v(11.64, -8.46) * mm});
            skArc(sketch, "E72.0.2", {"start": v(11.64, -8.46) * mm, "mid": v(13, -7.5) * mm, "end": v(13.15, -5.85) * mm});
            skLineSegment(sketch, "E72.0.3", {"start": v(13.15, -5.85) * mm, "end": v(11.14, 0) * mm});
            skLineSegment(sketch, "E72.0.4", {"start": v(11.14, 0) * mm, "end": v(13.15, 5.85) * mm});
            skArc(sketch, "E72.0.5", {"start": v(13.15, 5.85) * mm, "mid": v(13, 7.5) * mm, "end": v(11.64, 8.46) * mm});
            skLineSegment(sketch, "E72.0.6", {"start": v(11.64, 8.46) * mm, "end": v(5.57, 9.65) * mm});
            skLineSegment(sketch, "E72.0.7", {"start": v(5.57, 9.65) * mm, "end": v(1.5, 14.31) * mm});
            skArc(sketch, "E72.0.8", {"start": v(1.5, 14.31) * mm, "mid": v(0, 15) * mm, "end": v(-1.5, 14.31) * mm});
            skLineSegment(sketch, "E72.0.9", {"start": v(-1.5, 14.31) * mm, "end": v(-5.57, 9.65) * mm});
            skLineSegment(sketch, "E72.0.10", {"start": v(-5.57, 9.65) * mm, "end": v(-11.64, 8.46) * mm});
            skArc(sketch, "E72.0.11", {"start": v(-11.64, 8.46) * mm, "mid": v(-13, 7.5) * mm, "end": v(-13.15, 5.85) * mm});
            skLineSegment(sketch, "E72.0.12", {"start": v(-13.15, 5.85) * mm, "end": v(-11.14, 0) * mm});
            skLineSegment(sketch, "E72.0.13", {"start": v(-11.14, 0) * mm, "end": v(-13.15, -5.85) * mm});
            skArc(sketch, "E72.0.14", {"start": v(-13.15, -5.85) * mm, "mid": v(-13, -7.5) * mm, "end": v(-11.64, -8.46) * mm});
            skLineSegment(sketch, "E72.0.15", {"start": v(-11.64, -8.46) * mm, "end": v(-5.57, -9.65) * mm});
            skLineSegment(sketch, "E72.0.16", {"start": v(-5.57, -9.65) * mm, "end": v(-1.5, -14.31) * mm});
            skArc(sketch, "E72.0.17", {"start": v(-1.5, -14.31) * mm, "mid": v(0, -15) * mm, "end": v(1.5, -14.31) * mm});
            skLineSegment(sketch, "E73.0.0", {"start": v(0, -5.38) * mm, "end": v(1.87, -3.24) * mm});
            skLineSegment(sketch, "E73.0.1", {"start": v(1.87, -3.24) * mm, "end": v(4.66, -2.7) * mm});
            skLineSegment(sketch, "E73.0.2", {"start": v(4.66, -2.7) * mm, "end": v(3.74, 0) * mm});
            skLineSegment(sketch, "E73.0.3", {"start": v(3.74, 0) * mm, "end": v(4.66, 2.7) * mm});
            skLineSegment(sketch, "E73.0.4", {"start": v(4.66, 2.7) * mm, "end": v(1.87, 3.24) * mm});
            skLineSegment(sketch, "E73.0.5", {"start": v(1.87, 3.24) * mm, "end": v(0, 5.38) * mm});
            skLineSegment(sketch, "E73.0.6", {"start": v(0, 5.38) * mm, "end": v(-1.87, 3.24) * mm});
            skLineSegment(sketch, "E73.0.7", {"start": v(-1.87, 3.24) * mm, "end": v(-4.66, 2.7) * mm});
            skLineSegment(sketch, "E73.0.8", {"start": v(-4.66, 2.7) * mm, "end": v(-3.74, 0) * mm});
            skLineSegment(sketch, "E73.0.9", {"start": v(-3.74, 0) * mm, "end": v(-4.66, -2.7) * mm});
            skLineSegment(sketch, "E73.0.10", {"start": v(-4.66, -2.7) * mm, "end": v(-1.87, -3.24) * mm});
            skLineSegment(sketch, "E73.0.11", {"start": v(-1.87, -3.24) * mm, "end": v(0, -5.38) * mm});
            skSolve(sketch);
        }
        {
            var Q0;
            Q0=qCreatedBy(id+"F1.planeOp",FACE);
            cPlane(context, id + "F3", {"entities" : qUnion([Q0]), "cplaneType" : CPlaneType.OFFSET, "offset" : 2 * mm, "oppositeDirection" : true, "width" : 150 * mm, "height" : 150 * mm});
        }
        {
            var Q0;
            Q0=qCreatedBy(id+"F3.planeOp",FACE);
            var sketch = newSketch(context, id + "F4", { "sketchPlane" : qUnion([Q0])});
            skLineSegment(sketch, "E74.0.0", {"start": v(-19.93, 12.43) * mm, "end": v(-12.63, 13.33) * mm});
            skLineSegment(sketch, "E74.0.1", {"start": v(-12.63, 13.33) * mm, "end": v(-25.99, 27.5) * mm});
            skArc(sketch, "E74.0.2", {"start": v(-25.99, 27.5) * mm, "mid": v(-26.86, 28.05) * mm, "end": v(-27.89, 28.09) * mm});
            skLineSegment(sketch, "E74.0.3", {"start": v(-27.89, 28.09) * mm, "end": v(-40.67, 25.18) * mm});
            skArc(sketch, "E74.0.4", {"start": v(-40.67, 25.18) * mm, "mid": v(-41.96, 24.23) * mm, "end": v(-42.14, 22.64) * mm});
            skLineSegment(sketch, "E74.0.5", {"start": v(-42.14, 22.64) * mm, "end": v(-38.27, 10.1) * mm});
            skArc(sketch, "E74.0.6", {"start": v(-38.27, 10.1) * mm, "mid": v(-37.72, 9.24) * mm, "end": v(-36.81, 8.75) * mm});
            skLineSegment(sketch, "E74.0.7", {"start": v(-36.81, 8.75) * mm, "end": v(-17.86, 4.28) * mm});
            skLineSegment(sketch, "E74.0.8", {"start": v(-17.86, 4.28) * mm, "end": v(-20.73, 11.05) * mm});
            skArc(sketch, "E74.0.9", {"start": v(-20.73, 11.05) * mm, "mid": v(-20.68, 11.94) * mm, "end": v(-19.93, 12.43) * mm});
            skLineSegment(sketch, "E75.0.0", {"start": v(5.22, 17.6) * mm, "end": v(10.83, 36.26) * mm});
            skArc(sketch, "E75.0.1", {"start": v(10.83, 36.26) * mm, "mid": v(10.86, 37.28) * mm, "end": v(10.38, 38.2) * mm});
            skLineSegment(sketch, "E75.0.2", {"start": v(10.38, 38.2) * mm, "end": v(1.47, 47.81) * mm});
            skArc(sketch, "E75.0.3", {"start": v(1.47, 47.81) * mm, "mid": v(0, 48.45) * mm, "end": v(-1.47, 47.81) * mm});
            skLineSegment(sketch, "E75.0.4", {"start": v(-1.47, 47.81) * mm, "end": v(-10.38, 38.2) * mm});
            skArc(sketch, "E75.0.5", {"start": v(-10.38, 38.2) * mm, "mid": v(-10.86, 37.28) * mm, "end": v(-10.83, 36.26) * mm});
            skLineSegment(sketch, "E75.0.6", {"start": v(-10.83, 36.26) * mm, "end": v(-5.22, 17.6) * mm});
            skLineSegment(sketch, "E75.0.7", {"start": v(-5.22, 17.6) * mm, "end": v(-0.8, 23.48) * mm});
            skArc(sketch, "E75.0.8", {"start": v(-0.8, 23.48) * mm, "mid": v(0, 23.88) * mm, "end": v(0.8, 23.48) * mm});
            skLineSegment(sketch, "E75.0.9", {"start": v(0.8, 23.48) * mm, "end": v(5.22, 17.6) * mm});
            skLineSegment(sketch, "E76.0.0", {"start": v(20.73, 11.05) * mm, "end": v(17.86, 4.28) * mm});
            skLineSegment(sketch, "E76.0.1", {"start": v(17.86, 4.28) * mm, "end": v(36.81, 8.75) * mm});
            skArc(sketch, "E76.0.2", {"start": v(36.81, 8.75) * mm, "mid": v(37.72, 9.24) * mm, "end": v(38.27, 10.1) * mm});
            skLineSegment(sketch, "E76.0.3", {"start": v(38.27, 10.1) * mm, "end": v(42.14, 22.64) * mm});
            skArc(sketch, "E76.0.4", {"start": v(42.14, 22.64) * mm, "mid": v(41.96, 24.23) * mm, "end": v(40.67, 25.18) * mm});
            skLineSegment(sketch, "E76.0.5", {"start": v(40.67, 25.18) * mm, "end": v(27.89, 28.09) * mm});
            skArc(sketch, "E76.0.6", {"start": v(27.89, 28.09) * mm, "mid": v(26.86, 28.05) * mm, "end": v(25.99, 27.5) * mm});
            skLineSegment(sketch, "E76.0.7", {"start": v(25.99, 27.5) * mm, "end": v(12.63, 13.33) * mm});
            skLineSegment(sketch, "E76.0.8", {"start": v(12.63, 13.33) * mm, "end": v(19.93, 12.43) * mm});
            skArc(sketch, "E76.0.9", {"start": v(19.93, 12.43) * mm, "mid": v(20.68, 11.94) * mm, "end": v(20.73, 11.05) * mm});
            skLineSegment(sketch, "E77.0.0", {"start": v(19.93, -12.43) * mm, "end": v(12.63, -13.33) * mm});
            skLineSegment(sketch, "E77.0.1", {"start": v(12.63, -13.33) * mm, "end": v(25.99, -27.5) * mm});
            skArc(sketch, "E77.0.2", {"start": v(25.99, -27.5) * mm, "mid": v(26.86, -28.05) * mm, "end": v(27.89, -28.09) * mm});
            skLineSegment(sketch, "E77.0.3", {"start": v(27.89, -28.09) * mm, "end": v(40.67, -25.18) * mm});
            skArc(sketch, "E77.0.4", {"start": v(40.67, -25.18) * mm, "mid": v(41.96, -24.23) * mm, "end": v(42.14, -22.64) * mm});
            skLineSegment(sketch, "E77.0.5", {"start": v(42.14, -22.64) * mm, "end": v(38.27, -10.1) * mm});
            skArc(sketch, "E77.0.6", {"start": v(38.27, -10.1) * mm, "mid": v(37.72, -9.24) * mm, "end": v(36.81, -8.75) * mm});
            skLineSegment(sketch, "E77.0.7", {"start": v(36.81, -8.75) * mm, "end": v(17.86, -4.28) * mm});
            skLineSegment(sketch, "E77.0.8", {"start": v(17.86, -4.28) * mm, "end": v(20.73, -11.05) * mm});
            skArc(sketch, "E77.0.9", {"start": v(20.73, -11.05) * mm, "mid": v(20.68, -11.94) * mm, "end": v(19.93, -12.43) * mm});
            skLineSegment(sketch, "E78.0.0", {"start": v(-0.8, -23.48) * mm, "end": v(-5.22, -17.6) * mm});
            skLineSegment(sketch, "E78.0.1", {"start": v(-5.22, -17.6) * mm, "end": v(-10.83, -36.26) * mm});
            skArc(sketch, "E78.0.2", {"start": v(-10.83, -36.26) * mm, "mid": v(-10.86, -37.28) * mm, "end": v(-10.38, -38.2) * mm});
            skLineSegment(sketch, "E78.0.3", {"start": v(-10.38, -38.2) * mm, "end": v(-1.47, -47.81) * mm});
            skArc(sketch, "E78.0.4", {"start": v(-1.47, -47.81) * mm, "mid": v(0, -48.45) * mm, "end": v(1.47, -47.81) * mm});
            skLineSegment(sketch, "E78.0.5", {"start": v(1.47, -47.81) * mm, "end": v(10.38, -38.2) * mm});
            skArc(sketch, "E78.0.6", {"start": v(10.38, -38.2) * mm, "mid": v(10.86, -37.28) * mm, "end": v(10.83, -36.26) * mm});
            skLineSegment(sketch, "E78.0.7", {"start": v(10.83, -36.26) * mm, "end": v(5.22, -17.6) * mm});
            skLineSegment(sketch, "E78.0.8", {"start": v(5.22, -17.6) * mm, "end": v(0.8, -23.48) * mm});
            skArc(sketch, "E78.0.9", {"start": v(0.8, -23.48) * mm, "mid": v(0, -23.88) * mm, "end": v(-0.8, -23.48) * mm});
            skLineSegment(sketch, "E79.0.0", {"start": v(-20.73, -11.05) * mm, "end": v(-17.86, -4.28) * mm});
            skLineSegment(sketch, "E79.0.1", {"start": v(-17.86, -4.28) * mm, "end": v(-36.81, -8.75) * mm});
            skArc(sketch, "E79.0.2", {"start": v(-36.81, -8.75) * mm, "mid": v(-37.72, -9.24) * mm, "end": v(-38.27, -10.1) * mm});
            skLineSegment(sketch, "E79.0.3", {"start": v(-38.27, -10.1) * mm, "end": v(-42.14, -22.64) * mm});
            skArc(sketch, "E79.0.4", {"start": v(-42.14, -22.64) * mm, "mid": v(-41.96, -24.23) * mm, "end": v(-40.67, -25.18) * mm});
            skLineSegment(sketch, "E79.0.5", {"start": v(-40.67, -25.18) * mm, "end": v(-27.89, -28.09) * mm});
            skArc(sketch, "E79.0.6", {"start": v(-27.89, -28.09) * mm, "mid": v(-26.86, -28.05) * mm, "end": v(-25.99, -27.5) * mm});
            skLineSegment(sketch, "E79.0.7", {"start": v(-25.99, -27.5) * mm, "end": v(-12.63, -13.33) * mm});
            skLineSegment(sketch, "E79.0.8", {"start": v(-12.63, -13.33) * mm, "end": v(-19.93, -12.43) * mm});
            skArc(sketch, "E79.0.9", {"start": v(-19.93, -12.43) * mm, "mid": v(-20.68, -11.94) * mm, "end": v(-20.73, -11.05) * mm});
            skLineSegment(sketch, "E80.0.0", {"start": v(1.5, -14.31) * mm, "end": v(5.57, -9.65) * mm});
            skLineSegment(sketch, "E80.0.1", {"start": v(5.57, -9.65) * mm, "end": v(11.64, -8.46) * mm});
            skArc(sketch, "E80.0.2", {"start": v(11.64, -8.46) * mm, "mid": v(13, -7.5) * mm, "end": v(13.15, -5.85) * mm});
            skLineSegment(sketch, "E80.0.3", {"start": v(13.15, -5.85) * mm, "end": v(11.14, 0) * mm});
            skLineSegment(sketch, "E80.0.4", {"start": v(11.14, 0) * mm, "end": v(13.15, 5.85) * mm});
            skArc(sketch, "E80.0.5", {"start": v(13.15, 5.85) * mm, "mid": v(13, 7.5) * mm, "end": v(11.64, 8.46) * mm});
            skLineSegment(sketch, "E80.0.6", {"start": v(11.64, 8.46) * mm, "end": v(5.57, 9.65) * mm});
            skLineSegment(sketch, "E80.0.7", {"start": v(5.57, 9.65) * mm, "end": v(1.5, 14.31) * mm});
            skArc(sketch, "E80.0.8", {"start": v(1.5, 14.31) * mm, "mid": v(0, 15) * mm, "end": v(-1.5, 14.31) * mm});
            skLineSegment(sketch, "E80.0.9", {"start": v(-1.5, 14.31) * mm, "end": v(-5.57, 9.65) * mm});
            skLineSegment(sketch, "E80.0.10", {"start": v(-5.57, 9.65) * mm, "end": v(-11.64, 8.46) * mm});
            skArc(sketch, "E80.0.11", {"start": v(-11.64, 8.46) * mm, "mid": v(-13, 7.5) * mm, "end": v(-13.15, 5.85) * mm});
            skLineSegment(sketch, "E80.0.12", {"start": v(-13.15, 5.85) * mm, "end": v(-11.14, 0) * mm});
            skLineSegment(sketch, "E80.0.13", {"start": v(-11.14, 0) * mm, "end": v(-13.15, -5.85) * mm});
            skArc(sketch, "E80.0.14", {"start": v(-13.15, -5.85) * mm, "mid": v(-13, -7.5) * mm, "end": v(-11.64, -8.46) * mm});
            skLineSegment(sketch, "E80.0.15", {"start": v(-11.64, -8.46) * mm, "end": v(-5.57, -9.65) * mm});
            skLineSegment(sketch, "E80.0.16", {"start": v(-5.57, -9.65) * mm, "end": v(-1.5, -14.31) * mm});
            skArc(sketch, "E80.0.17", {"start": v(-1.5, -14.31) * mm, "mid": v(0, -15) * mm, "end": v(1.5, -14.31) * mm});
            skLineSegment(sketch, "E81.0.0", {"start": v(0, -5.38) * mm, "end": v(1.87, -3.24) * mm});
            skLineSegment(sketch, "E81.0.1", {"start": v(1.87, -3.24) * mm, "end": v(4.66, -2.7) * mm});
            skLineSegment(sketch, "E81.0.2", {"start": v(4.66, -2.7) * mm, "end": v(3.74, 0) * mm});
            skLineSegment(sketch, "E81.0.3", {"start": v(3.74, 0) * mm, "end": v(4.66, 2.7) * mm});
            skLineSegment(sketch, "E81.0.4", {"start": v(4.66, 2.7) * mm, "end": v(1.87, 3.24) * mm});
            skLineSegment(sketch, "E81.0.5", {"start": v(1.87, 3.24) * mm, "end": v(0, 5.38) * mm});
            skLineSegment(sketch, "E81.0.6", {"start": v(0, 5.38) * mm, "end": v(-1.87, 3.24) * mm});
            skLineSegment(sketch, "E81.0.7", {"start": v(-1.87, 3.24) * mm, "end": v(-4.66, 2.7) * mm});
            skLineSegment(sketch, "E81.0.8", {"start": v(-4.66, 2.7) * mm, "end": v(-3.74, 0) * mm});
            skLineSegment(sketch, "E81.0.9", {"start": v(-3.74, 0) * mm, "end": v(-4.66, -2.7) * mm});
            skLineSegment(sketch, "E81.0.10", {"start": v(-4.66, -2.7) * mm, "end": v(-1.87, -3.24) * mm});
            skLineSegment(sketch, "E81.0.11", {"start": v(-1.87, -3.24) * mm, "end": v(0, -5.38) * mm});
            skSolve(sketch);
        }
        {
            var Q0;
            Q0 = qSketchRegion(id + "F0", true);
            var Q1;
            Q1 = qSketchRegion(id + "F2", true);
            var Q2;
            Q2 = qSketchRegion(id + "F4", true);
            extrude(context, id + "F5", {"entities" : qUnion([Q0, Q1, Q2]), "depth" : 3 * mm, "offsetDistance" : 25 * mm});
        }
        {
            var Q0;
            Q0=makeQuery(id+"F5.opExtrude","CAP_FACE",FACE,{"disambiguationData":[OSD([sQuery(id+"F4.wireOp",EDGE,"E80.0.0"),sQuery(id+"F4.wireOp",EDGE,"E80.0.1"),sQuery(id+"F4.wireOp",EDGE,"E80.0.2"),sQuery(id+"F4.wireOp",EDGE,"E80.0.3"),sQuery(id+"F4.wireOp",EDGE,"E80.0.4"),sQuery(id+"F4.wireOp",EDGE,"E80.0.5"),sQuery(id+"F4.wireOp",EDGE,"E80.0.6"),sQuery(id+"F4.wireOp",EDGE,"E80.0.7"),sQuery(id+"F4.wireOp",EDGE,"E80.0.8"),sQuery(id+"F4.wireOp",EDGE,"E80.0.9"),sQuery(id+"F4.wireOp",EDGE,"E80.0.10"),sQuery(id+"F4.wireOp",EDGE,"E80.0.11"),sQuery(id+"F4.wireOp",EDGE,"E80.0.12"),sQuery(id+"F4.wireOp",EDGE,"E80.0.13"),sQuery(id+"F4.wireOp",EDGE,"E80.0.14"),sQuery(id+"F4.wireOp",EDGE,"E80.0.15"),sQuery(id+"F4.wireOp",EDGE,"E80.0.16"),sQuery(id+"F4.wireOp",EDGE,"E80.0.17"),sQuery(id+"F4.wireOp",EDGE,"E81.0.0"),sQuery(id+"F4.wireOp",EDGE,"E81.0.1"),sQuery(id+"F4.wireOp",EDGE,"E81.0.2"),sQuery(id+"F4.wireOp",EDGE,"E81.0.3"),sQuery(id+"F4.wireOp",EDGE,"E81.0.4"),sQuery(id+"F4.wireOp",EDGE,"E81.0.5"),sQuery(id+"F4.wireOp",EDGE,"E81.0.6"),sQuery(id+"F4.wireOp",EDGE,"E81.0.7"),sQuery(id+"F4.wireOp",EDGE,"E81.0.8"),sQuery(id+"F4.wireOp",EDGE,"E81.0.9"),sQuery(id+"F4.wireOp",EDGE,"E81.0.10"),sQuery(id+"F4.wireOp",EDGE,"E81.0.11")])],"isStart":true});
            fillet(context, id + "F6", {"entities" : qUnion([Q0]), "radius" : 1 * mm, "tangentPropagation" : true, "allowEdgeOverflow" : false});
        }
        {
            var Q0;
            Q0=makeQuery(id+"F5.opExtrude","CAP_FACE",FACE,{"disambiguationData":[OSD([sQuery(id+"F4.wireOp",EDGE,"E77.0.0"),sQuery(id+"F4.wireOp",EDGE,"E77.0.1"),sQuery(id+"F4.wireOp",EDGE,"E77.0.2"),sQuery(id+"F4.wireOp",EDGE,"E77.0.3"),sQuery(id+"F4.wireOp",EDGE,"E77.0.4"),sQuery(id+"F4.wireOp",EDGE,"E77.0.5"),sQuery(id+"F4.wireOp",EDGE,"E77.0.6"),sQuery(id+"F4.wireOp",EDGE,"E77.0.7"),sQuery(id+"F4.wireOp",EDGE,"E77.0.8"),sQuery(id+"F4.wireOp",EDGE,"E77.0.9")])],"isStart":true});
            var Q1;
            Q1=makeQuery(id+"F5.opExtrude","CAP_FACE",FACE,{"disambiguationData":[OSD([sQuery(id+"F4.wireOp",EDGE,"E76.0.0"),sQuery(id+"F4.wireOp",EDGE,"E76.0.1"),sQuery(id+"F4.wireOp",EDGE,"E76.0.2"),sQuery(id+"F4.wireOp",EDGE,"E76.0.3"),sQuery(id+"F4.wireOp",EDGE,"E76.0.4"),sQuery(id+"F4.wireOp",EDGE,"E76.0.5"),sQuery(id+"F4.wireOp",EDGE,"E76.0.6"),sQuery(id+"F4.wireOp",EDGE,"E76.0.7"),sQuery(id+"F4.wireOp",EDGE,"E76.0.8"),sQuery(id+"F4.wireOp",EDGE,"E76.0.9")])],"isStart":true});
            var Q2;
            Q2=makeQuery(id+"F5.opExtrude","CAP_FACE",FACE,{"disambiguationData":[OSD([sQuery(id+"F4.wireOp",EDGE,"E75.0.0"),sQuery(id+"F4.wireOp",EDGE,"E75.0.1"),sQuery(id+"F4.wireOp",EDGE,"E75.0.2"),sQuery(id+"F4.wireOp",EDGE,"E75.0.3"),sQuery(id+"F4.wireOp",EDGE,"E75.0.4"),sQuery(id+"F4.wireOp",EDGE,"E75.0.5"),sQuery(id+"F4.wireOp",EDGE,"E75.0.6"),sQuery(id+"F4.wireOp",EDGE,"E75.0.7"),sQuery(id+"F4.wireOp",EDGE,"E75.0.8"),sQuery(id+"F4.wireOp",EDGE,"E75.0.9")])],"isStart":true});
            var Q3;
            Q3=makeQuery(id+"F5.opExtrude","CAP_FACE",FACE,{"disambiguationData":[OSD([sQuery(id+"F4.wireOp",EDGE,"E74.0.0"),sQuery(id+"F4.wireOp",EDGE,"E74.0.1"),sQuery(id+"F4.wireOp",EDGE,"E74.0.2"),sQuery(id+"F4.wireOp",EDGE,"E74.0.3"),sQuery(id+"F4.wireOp",EDGE,"E74.0.4"),sQuery(id+"F4.wireOp",EDGE,"E74.0.5"),sQuery(id+"F4.wireOp",EDGE,"E74.0.6"),sQuery(id+"F4.wireOp",EDGE,"E74.0.7"),sQuery(id+"F4.wireOp",EDGE,"E74.0.8"),sQuery(id+"F4.wireOp",EDGE,"E74.0.9")])],"isStart":true});
            var Q4;
            Q4=makeQuery(id+"F5.opExtrude","CAP_FACE",FACE,{"disambiguationData":[OSD([sQuery(id+"F4.wireOp",EDGE,"E79.0.0"),sQuery(id+"F4.wireOp",EDGE,"E79.0.1"),sQuery(id+"F4.wireOp",EDGE,"E79.0.2"),sQuery(id+"F4.wireOp",EDGE,"E79.0.3"),sQuery(id+"F4.wireOp",EDGE,"E79.0.4"),sQuery(id+"F4.wireOp",EDGE,"E79.0.5"),sQuery(id+"F4.wireOp",EDGE,"E79.0.6"),sQuery(id+"F4.wireOp",EDGE,"E79.0.7"),sQuery(id+"F4.wireOp",EDGE,"E79.0.8"),sQuery(id+"F4.wireOp",EDGE,"E79.0.9")])],"isStart":true});
            var Q5;
            Q5=makeQuery(id+"F5.opExtrude","CAP_FACE",FACE,{"disambiguationData":[OSD([sQuery(id+"F4.wireOp",EDGE,"E78.0.0"),sQuery(id+"F4.wireOp",EDGE,"E78.0.1"),sQuery(id+"F4.wireOp",EDGE,"E78.0.2"),sQuery(id+"F4.wireOp",EDGE,"E78.0.3"),sQuery(id+"F4.wireOp",EDGE,"E78.0.4"),sQuery(id+"F4.wireOp",EDGE,"E78.0.5"),sQuery(id+"F4.wireOp",EDGE,"E78.0.6"),sQuery(id+"F4.wireOp",EDGE,"E78.0.7"),sQuery(id+"F4.wireOp",EDGE,"E78.0.8"),sQuery(id+"F4.wireOp",EDGE,"E78.0.9")])],"isStart":true});
            fillet(context, id + "F7", {"entities" : qUnion([Q0, Q1, Q2, Q3, Q4, Q5]), "radius" : 1 * mm, "tangentPropagation" : true, "allowEdgeOverflow" : false});
        }
        {
            var Q0;
            Q0=makeQuery(id+"F5.opExtrude","CAP_FACE",FACE,{"disambiguationData":[OSD([sQuery(id+"F2.wireOp",EDGE,"E65.0.0"),sQuery(id+"F2.wireOp",EDGE,"E65.0.1"),sQuery(id+"F2.wireOp",EDGE,"E65.0.2"),sQuery(id+"F2.wireOp",EDGE,"E65.0.3"),sQuery(id+"F2.wireOp",EDGE,"E65.0.4"),sQuery(id+"F2.wireOp",EDGE,"E65.0.5"),sQuery(id+"F2.wireOp",EDGE,"E65.0.6"),sQuery(id+"F2.wireOp",EDGE,"E65.0.7"),sQuery(id+"F2.wireOp",EDGE,"E65.0.8"),sQuery(id+"F2.wireOp",EDGE,"E65.0.9"),sQuery(id+"F2.wireOp",EDGE,"E65.0.10"),sQuery(id+"F2.wireOp",EDGE,"E65.0.11"),sQuery(id+"F2.wireOp",EDGE,"E65.0.12"),sQuery(id+"F2.wireOp",EDGE,"E65.0.13"),sQuery(id+"F2.wireOp",EDGE,"E65.0.14"),sQuery(id+"F2.wireOp",EDGE,"E65.0.15"),sQuery(id+"F2.wireOp",EDGE,"E65.0.16"),sQuery(id+"F2.wireOp",EDGE,"E65.0.17"),sQuery(id+"F2.wireOp",EDGE,"E65.0.18"),sQuery(id+"F2.wireOp",EDGE,"E65.0.19"),sQuery(id+"F2.wireOp",EDGE,"E65.0.20"),sQuery(id+"F2.wireOp",EDGE,"E65.0.21"),sQuery(id+"F2.wireOp",EDGE,"E65.0.22"),sQuery(id+"F2.wireOp",EDGE,"E65.0.23"),sQuery(id+"F2.wireOp",EDGE,"E65.0.24"),sQuery(id+"F2.wireOp",EDGE,"E65.0.25"),sQuery(id+"F2.wireOp",EDGE,"E65.0.26"),sQuery(id+"F2.wireOp",EDGE,"E65.0.27"),sQuery(id+"F2.wireOp",EDGE,"E65.0.28"),sQuery(id+"F2.wireOp",EDGE,"E65.0.29"),sQuery(id+"F2.wireOp",EDGE,"E65.0.30"),sQuery(id+"F2.wireOp",EDGE,"E65.0.31"),sQuery(id+"F2.wireOp",EDGE,"E65.0.32"),sQuery(id+"F2.wireOp",EDGE,"E65.0.33"),sQuery(id+"F2.wireOp",EDGE,"E65.0.34"),sQuery(id+"F2.wireOp",EDGE,"E65.0.35"),sQuery(id+"F2.wireOp",EDGE,"E65.0.36"),sQuery(id+"F2.wireOp",EDGE,"E65.0.37"),sQuery(id+"F2.wireOp",EDGE,"E65.0.38"),sQuery(id+"F2.wireOp",EDGE,"E65.0.39"),sQuery(id+"F2.wireOp",EDGE,"E65.0.40"),sQuery(id+"F2.wireOp",EDGE,"E65.0.41"),sQuery(id+"F2.wireOp",EDGE,"E66.0.0"),sQuery(id+"F2.wireOp",EDGE,"E66.0.1"),sQuery(id+"F2.wireOp",EDGE,"E66.0.2"),sQuery(id+"F2.wireOp",EDGE,"E66.0.3"),sQuery(id+"F2.wireOp",EDGE,"E66.0.4"),sQuery(id+"F2.wireOp",EDGE,"E66.0.5"),sQuery(id+"F2.wireOp",EDGE,"E66.0.6"),sQuery(id+"F2.wireOp",EDGE,"E66.0.7"),sQuery(id+"F2.wireOp",EDGE,"E66.0.8"),sQuery(id+"F2.wireOp",EDGE,"E66.0.9"),sQuery(id+"F2.wireOp",EDGE,"E67.0.0"),sQuery(id+"F2.wireOp",EDGE,"E67.0.1"),sQuery(id+"F2.wireOp",EDGE,"E67.0.2"),sQuery(id+"F2.wireOp",EDGE,"E67.0.3"),sQuery(id+"F2.wireOp",EDGE,"E67.0.4"),sQuery(id+"F2.wireOp",EDGE,"E67.0.5"),sQuery(id+"F2.wireOp",EDGE,"E67.0.6"),sQuery(id+"F2.wireOp",EDGE,"E67.0.7"),sQuery(id+"F2.wireOp",EDGE,"E67.0.8"),sQuery(id+"F2.wireOp",EDGE,"E67.0.9"),sQuery(id+"F2.wireOp",EDGE,"E68.0.0"),sQuery(id+"F2.wireOp",EDGE,"E68.0.1"),sQuery(id+"F2.wireOp",EDGE,"E68.0.2"),sQuery(id+"F2.wireOp",EDGE,"E68.0.3"),sQuery(id+"F2.wireOp",EDGE,"E68.0.4"),sQuery(id+"F2.wireOp",EDGE,"E68.0.5"),sQuery(id+"F2.wireOp",EDGE,"E68.0.6"),sQuery(id+"F2.wireOp",EDGE,"E68.0.7"),sQuery(id+"F2.wireOp",EDGE,"E68.0.8"),sQuery(id+"F2.wireOp",EDGE,"E68.0.9"),sQuery(id+"F2.wireOp",EDGE,"E69.0.0"),sQuery(id+"F2.wireOp",EDGE,"E69.0.1"),sQuery(id+"F2.wireOp",EDGE,"E69.0.2"),sQuery(id+"F2.wireOp",EDGE,"E69.0.3"),sQuery(id+"F2.wireOp",EDGE,"E69.0.4"),sQuery(id+"F2.wireOp",EDGE,"E69.0.5"),sQuery(id+"F2.wireOp",EDGE,"E69.0.6"),sQuery(id+"F2.wireOp",EDGE,"E69.0.7"),sQuery(id+"F2.wireOp",EDGE,"E69.0.8"),sQuery(id+"F2.wireOp",EDGE,"E69.0.9"),sQuery(id+"F2.wireOp",EDGE,"E70.0.0"),sQuery(id+"F2.wireOp",EDGE,"E70.0.1"),sQuery(id+"F2.wireOp",EDGE,"E70.0.2"),sQuery(id+"F2.wireOp",EDGE,"E70.0.3"),sQuery(id+"F2.wireOp",EDGE,"E70.0.4"),sQuery(id+"F2.wireOp",EDGE,"E70.0.5"),sQuery(id+"F2.wireOp",EDGE,"E70.0.6"),sQuery(id+"F2.wireOp",EDGE,"E70.0.7"),sQuery(id+"F2.wireOp",EDGE,"E70.0.8"),sQuery(id+"F2.wireOp",EDGE,"E70.0.9"),sQuery(id+"F2.wireOp",EDGE,"E71.0.0"),sQuery(id+"F2.wireOp",EDGE,"E71.0.1"),sQuery(id+"F2.wireOp",EDGE,"E71.0.2"),sQuery(id+"F2.wireOp",EDGE,"E71.0.3"),sQuery(id+"F2.wireOp",EDGE,"E71.0.4"),sQuery(id+"F2.wireOp",EDGE,"E71.0.5"),sQuery(id+"F2.wireOp",EDGE,"E71.0.6"),sQuery(id+"F2.wireOp",EDGE,"E71.0.7"),sQuery(id+"F2.wireOp",EDGE,"E71.0.8"),sQuery(id+"F2.wireOp",EDGE,"E71.0.9"),sQuery(id+"F2.wireOp",EDGE,"E72.0.0"),sQuery(id+"F2.wireOp",EDGE,"E72.0.1"),sQuery(id+"F2.wireOp",EDGE,"E72.0.2"),sQuery(id+"F2.wireOp",EDGE,"E72.0.3"),sQuery(id+"F2.wireOp",EDGE,"E72.0.4"),sQuery(id+"F2.wireOp",EDGE,"E72.0.5"),sQuery(id+"F2.wireOp",EDGE,"E72.0.6"),sQuery(id+"F2.wireOp",EDGE,"E72.0.7"),sQuery(id+"F2.wireOp",EDGE,"E72.0.8"),sQuery(id+"F2.wireOp",EDGE,"E72.0.9"),sQuery(id+"F2.wireOp",EDGE,"E72.0.10"),sQuery(id+"F2.wireOp",EDGE,"E72.0.11"),sQuery(id+"F2.wireOp",EDGE,"E72.0.12"),sQuery(id+"F2.wireOp",EDGE,"E72.0.13"),sQuery(id+"F2.wireOp",EDGE,"E72.0.14"),sQuery(id+"F2.wireOp",EDGE,"E72.0.15"),sQuery(id+"F2.wireOp",EDGE,"E72.0.16"),sQuery(id+"F2.wireOp",EDGE,"E72.0.17")])],"isStart":true});
            fillet(context, id + "F8", {"entities" : qUnion([Q0]), "radius" : 1 * mm, "tangentPropagation" : true, "allowEdgeOverflow" : false});
        }
        {
            var Q0;
            Q0=makeQuery(id+"F5.opExtrude","CAP_EDGE",EDGE,{"disambiguationData":[OSD([sQuery(id+"F0.wireOp",EDGE,"E57")])],"isStart":true});
            var Q1;
            Q1=makeQuery(id+"F5.opExtrude","CAP_EDGE",EDGE,{"disambiguationData":[OSD([sQuery(id+"F0.wireOp",EDGE,"E58.1.0")])],"isStart":true});
            var Q2;
            Q2=makeQuery(id+"F5.opExtrude","CAP_EDGE",EDGE,{"disambiguationData":[OSD([sQuery(id+"F0.wireOp",EDGE,"E58.2.0")])],"isStart":true});
            var Q3;
            Q3=makeQuery(id+"F5.opExtrude","CAP_EDGE",EDGE,{"disambiguationData":[OSD([sQuery(id+"F0.wireOp",EDGE,"E58.3.0")])],"isStart":true});
            var Q4;
            Q4=makeQuery(id+"F5.opExtrude","CAP_EDGE",EDGE,{"disambiguationData":[OSD([sQuery(id+"F0.wireOp",EDGE,"E58.4.0")])],"isStart":true});
            var Q5;
            Q5=makeQuery(id+"F5.opExtrude","CAP_EDGE",EDGE,{"disambiguationData":[OSD([sQuery(id+"F0.wireOp",EDGE,"E58.5.0")])],"isStart":true});
            fillet(context, id + "F9", {"entities" : qUnion([Q0, Q1, Q2, Q3, Q4, Q5]), "radius" : 1 * mm, "tangentPropagation" : true, "allowEdgeOverflow" : false});
        }
        {
            var Q0;
            Q0=makeQuery(id+"F5.opExtrude","CAP_FACE",FACE,{"disambiguationData":[OSD([sQuery(id+"F4.wireOp",EDGE,"E76.0.0"),sQuery(id+"F4.wireOp",EDGE,"E76.0.1"),sQuery(id+"F4.wireOp",EDGE,"E76.0.2"),sQuery(id+"F4.wireOp",EDGE,"E76.0.3"),sQuery(id+"F4.wireOp",EDGE,"E76.0.4"),sQuery(id+"F4.wireOp",EDGE,"E76.0.5"),sQuery(id+"F4.wireOp",EDGE,"E76.0.6"),sQuery(id+"F4.wireOp",EDGE,"E76.0.7"),sQuery(id+"F4.wireOp",EDGE,"E76.0.8"),sQuery(id+"F4.wireOp",EDGE,"E76.0.9")])],"isStart":false});
            var Q1;
            Q1=makeQuery(id+"F5.opExtrude","CAP_FACE",FACE,{"disambiguationData":[OSD([sQuery(id+"F4.wireOp",EDGE,"E77.0.0"),sQuery(id+"F4.wireOp",EDGE,"E77.0.1"),sQuery(id+"F4.wireOp",EDGE,"E77.0.2"),sQuery(id+"F4.wireOp",EDGE,"E77.0.3"),sQuery(id+"F4.wireOp",EDGE,"E77.0.4"),sQuery(id+"F4.wireOp",EDGE,"E77.0.5"),sQuery(id+"F4.wireOp",EDGE,"E77.0.6"),sQuery(id+"F4.wireOp",EDGE,"E77.0.7"),sQuery(id+"F4.wireOp",EDGE,"E77.0.8"),sQuery(id+"F4.wireOp",EDGE,"E77.0.9")])],"isStart":false});
            var Q2;
            Q2=makeQuery(id+"F5.opExtrude","CAP_FACE",FACE,{"disambiguationData":[OSD([sQuery(id+"F4.wireOp",EDGE,"E78.0.0"),sQuery(id+"F4.wireOp",EDGE,"E78.0.1"),sQuery(id+"F4.wireOp",EDGE,"E78.0.2"),sQuery(id+"F4.wireOp",EDGE,"E78.0.3"),sQuery(id+"F4.wireOp",EDGE,"E78.0.4"),sQuery(id+"F4.wireOp",EDGE,"E78.0.5"),sQuery(id+"F4.wireOp",EDGE,"E78.0.6"),sQuery(id+"F4.wireOp",EDGE,"E78.0.7"),sQuery(id+"F4.wireOp",EDGE,"E78.0.8"),sQuery(id+"F4.wireOp",EDGE,"E78.0.9")])],"isStart":false});
            var Q3;
            Q3=makeQuery(id+"F5.opExtrude","CAP_FACE",FACE,{"disambiguationData":[OSD([sQuery(id+"F4.wireOp",EDGE,"E79.0.0"),sQuery(id+"F4.wireOp",EDGE,"E79.0.1"),sQuery(id+"F4.wireOp",EDGE,"E79.0.2"),sQuery(id+"F4.wireOp",EDGE,"E79.0.3"),sQuery(id+"F4.wireOp",EDGE,"E79.0.4"),sQuery(id+"F4.wireOp",EDGE,"E79.0.5"),sQuery(id+"F4.wireOp",EDGE,"E79.0.6"),sQuery(id+"F4.wireOp",EDGE,"E79.0.7"),sQuery(id+"F4.wireOp",EDGE,"E79.0.8"),sQuery(id+"F4.wireOp",EDGE,"E79.0.9")])],"isStart":false});
            var Q4;
            Q4=makeQuery(id+"F5.opExtrude","CAP_FACE",FACE,{"disambiguationData":[OSD([sQuery(id+"F4.wireOp",EDGE,"E74.0.0"),sQuery(id+"F4.wireOp",EDGE,"E74.0.1"),sQuery(id+"F4.wireOp",EDGE,"E74.0.2"),sQuery(id+"F4.wireOp",EDGE,"E74.0.3"),sQuery(id+"F4.wireOp",EDGE,"E74.0.4"),sQuery(id+"F4.wireOp",EDGE,"E74.0.5"),sQuery(id+"F4.wireOp",EDGE,"E74.0.6"),sQuery(id+"F4.wireOp",EDGE,"E74.0.7"),sQuery(id+"F4.wireOp",EDGE,"E74.0.8"),sQuery(id+"F4.wireOp",EDGE,"E74.0.9")])],"isStart":false});
            var Q5;
            Q5=makeQuery(id+"F5.opExtrude","CAP_FACE",FACE,{"disambiguationData":[OSD([sQuery(id+"F4.wireOp",EDGE,"E75.0.0"),sQuery(id+"F4.wireOp",EDGE,"E75.0.1"),sQuery(id+"F4.wireOp",EDGE,"E75.0.2"),sQuery(id+"F4.wireOp",EDGE,"E75.0.3"),sQuery(id+"F4.wireOp",EDGE,"E75.0.4"),sQuery(id+"F4.wireOp",EDGE,"E75.0.5"),sQuery(id+"F4.wireOp",EDGE,"E75.0.6"),sQuery(id+"F4.wireOp",EDGE,"E75.0.7"),sQuery(id+"F4.wireOp",EDGE,"E75.0.8"),sQuery(id+"F4.wireOp",EDGE,"E75.0.9")])],"isStart":false});
            fillet(context, id + "F10", {"entities" : qUnion([Q0, Q1, Q2, Q3, Q4, Q5]), "radius" : 1 * mm, "tangentPropagation" : true, "allowEdgeOverflow" : false});
        }
        {
            var Q0;
            Q0=makeQuery(id+"F5.opExtrude","CAP_EDGE",EDGE,{"disambiguationData":[OSD([sQuery(id+"F2.wireOp",EDGE,"E65.0.28")])],"isStart":false});
            fillet(context, id + "F11", {"entities" : qUnion([Q0]), "radius" : 1 * mm, "tangentPropagation" : true, "allowEdgeOverflow" : false});
        }
        {
            var Q0;
            Q0=makeQuery(id+"F5.opExtrude","CAP_EDGE",EDGE,{"disambiguationData":[OSD([sQuery(id+"F0.wireOp",EDGE,"E1")])],"isStart":false});
            var Q1;
            Q1=makeQuery(id+"F5.opExtrude","CAP_EDGE",EDGE,{"disambiguationData":[OSD([sQuery(id+"F0.wireOp",EDGE,"E7.5.4")])],"isStart":false});
            var Q2;
            Q2=makeQuery(id+"F5.opExtrude","CAP_EDGE",EDGE,{"disambiguationData":[OSD([sQuery(id+"F0.wireOp",EDGE,"E7.4.4")])],"isStart":false});
            var Q3;
            Q3=makeQuery(id+"F5.opExtrude","CAP_EDGE",EDGE,{"disambiguationData":[OSD([sQuery(id+"F0.wireOp",EDGE,"E7.3.4")])],"isStart":false});
            var Q4;
            Q4=makeQuery(id+"F5.opExtrude","CAP_EDGE",EDGE,{"disambiguationData":[OSD([sQuery(id+"F0.wireOp",EDGE,"E7.2.4")])],"isStart":false});
            var Q5;
            Q5=makeQuery(id+"F5.opExtrude","CAP_EDGE",EDGE,{"disambiguationData":[OSD([sQuery(id+"F0.wireOp",EDGE,"E7.1.4")])],"isStart":false});
            fillet(context, id + "F12", {"entities" : qUnion([Q0, Q1, Q2, Q3, Q4, Q5]), "radius" : 1 * mm, "tangentPropagation" : true, "allowEdgeOverflow" : false});
        }
        {
            var Q0;
            Q0=makeQuery(id+"F5.opExtrude","CAP_EDGE",EDGE,{"disambiguationData":[OSD([sQuery(id+"F2.wireOp",EDGE,"E67.0.1")])],"isStart":false});
            var Q1;
            Q1=makeQuery(id+"F5.opExtrude","CAP_EDGE",EDGE,{"disambiguationData":[OSD([sQuery(id+"F2.wireOp",EDGE,"E68.0.1")])],"isStart":false});
            var Q2;
            Q2=makeQuery(id+"F5.opExtrude","CAP_EDGE",EDGE,{"disambiguationData":[OSD([sQuery(id+"F2.wireOp",EDGE,"E69.0.1")])],"isStart":false});
            var Q3;
            Q3=makeQuery(id+"F5.opExtrude","CAP_EDGE",EDGE,{"disambiguationData":[OSD([sQuery(id+"F2.wireOp",EDGE,"E70.0.0")])],"isStart":false});
            var Q4;
            Q4=makeQuery(id+"F5.opExtrude","CAP_EDGE",EDGE,{"disambiguationData":[OSD([sQuery(id+"F2.wireOp",EDGE,"E71.0.1")])],"isStart":false});
            var Q5;
            Q5=makeQuery(id+"F5.opExtrude","CAP_EDGE",EDGE,{"disambiguationData":[OSD([sQuery(id+"F2.wireOp",EDGE,"E66.0.1")])],"isStart":false});
            var Q6;
            Q6=makeQuery(id+"F5.opExtrude","CAP_EDGE",EDGE,{"disambiguationData":[OSD([sQuery(id+"F2.wireOp",EDGE,"E66.0.0")])],"isStart":false});
            var Q7;
            Q7=makeQuery(id+"F5.opExtrude","CAP_EDGE",EDGE,{"disambiguationData":[OSD([sQuery(id+"F2.wireOp",EDGE,"E67.0.0")])],"isStart":false});
            var Q8;
            Q8=makeQuery(id+"F5.opExtrude","CAP_EDGE",EDGE,{"disambiguationData":[OSD([sQuery(id+"F2.wireOp",EDGE,"E68.0.0")])],"isStart":false});
            var Q9;
            Q9=makeQuery(id+"F5.opExtrude","CAP_EDGE",EDGE,{"disambiguationData":[OSD([sQuery(id+"F2.wireOp",EDGE,"E69.0.0")])],"isStart":false});
            var Q10;
            Q10=makeQuery(id+"F5.opExtrude","CAP_EDGE",EDGE,{"disambiguationData":[OSD([sQuery(id+"F2.wireOp",EDGE,"E70.0.9")])],"isStart":false});
            var Q11;
            Q11=makeQuery(id+"F5.opExtrude","CAP_EDGE",EDGE,{"disambiguationData":[OSD([sQuery(id+"F2.wireOp",EDGE,"E71.0.0")])],"isStart":false});
            var Q12;
            Q12=makeQuery(id+"F5.opExtrude","CAP_EDGE",EDGE,{"disambiguationData":[OSD([sQuery(id+"F2.wireOp",EDGE,"E72.0.4")])],"isStart":false});
            fillet(context, id + "F13", {"entities" : qUnion([Q0, Q1, Q2, Q3, Q4, Q5, Q6, Q7, Q8, Q9, Q10, Q11, Q12]), "radius" : 1 * mm, "tangentPropagation" : true, "allowEdgeOverflow" : false});
        }
        {
            var Q0;
            Q0=makeQuery(id+"F5.opExtrude","CAP_FACE",FACE,{"disambiguationData":[OSD([sQuery(id+"F2.wireOp",EDGE,"E65.0.0"),sQuery(id+"F2.wireOp",EDGE,"E65.0.1"),sQuery(id+"F2.wireOp",EDGE,"E65.0.2"),sQuery(id+"F2.wireOp",EDGE,"E65.0.3"),sQuery(id+"F2.wireOp",EDGE,"E65.0.4"),sQuery(id+"F2.wireOp",EDGE,"E65.0.5"),sQuery(id+"F2.wireOp",EDGE,"E65.0.6"),sQuery(id+"F2.wireOp",EDGE,"E65.0.7"),sQuery(id+"F2.wireOp",EDGE,"E65.0.8"),sQuery(id+"F2.wireOp",EDGE,"E65.0.9"),sQuery(id+"F2.wireOp",EDGE,"E65.0.10"),sQuery(id+"F2.wireOp",EDGE,"E65.0.11"),sQuery(id+"F2.wireOp",EDGE,"E65.0.12"),sQuery(id+"F2.wireOp",EDGE,"E65.0.13"),sQuery(id+"F2.wireOp",EDGE,"E65.0.14"),sQuery(id+"F2.wireOp",EDGE,"E65.0.15"),sQuery(id+"F2.wireOp",EDGE,"E65.0.16"),sQuery(id+"F2.wireOp",EDGE,"E65.0.17"),sQuery(id+"F2.wireOp",EDGE,"E65.0.18"),sQuery(id+"F2.wireOp",EDGE,"E65.0.19"),sQuery(id+"F2.wireOp",EDGE,"E65.0.20"),sQuery(id+"F2.wireOp",EDGE,"E65.0.21"),sQuery(id+"F2.wireOp",EDGE,"E65.0.22"),sQuery(id+"F2.wireOp",EDGE,"E65.0.23"),sQuery(id+"F2.wireOp",EDGE,"E65.0.24"),sQuery(id+"F2.wireOp",EDGE,"E65.0.25"),sQuery(id+"F2.wireOp",EDGE,"E65.0.26"),sQuery(id+"F2.wireOp",EDGE,"E65.0.27"),sQuery(id+"F2.wireOp",EDGE,"E65.0.28"),sQuery(id+"F2.wireOp",EDGE,"E65.0.29"),sQuery(id+"F2.wireOp",EDGE,"E65.0.30"),sQuery(id+"F2.wireOp",EDGE,"E65.0.31"),sQuery(id+"F2.wireOp",EDGE,"E65.0.32"),sQuery(id+"F2.wireOp",EDGE,"E65.0.33"),sQuery(id+"F2.wireOp",EDGE,"E65.0.34"),sQuery(id+"F2.wireOp",EDGE,"E65.0.35"),sQuery(id+"F2.wireOp",EDGE,"E65.0.36"),sQuery(id+"F2.wireOp",EDGE,"E65.0.37"),sQuery(id+"F2.wireOp",EDGE,"E65.0.38"),sQuery(id+"F2.wireOp",EDGE,"E65.0.39"),sQuery(id+"F2.wireOp",EDGE,"E65.0.40"),sQuery(id+"F2.wireOp",EDGE,"E65.0.41"),sQuery(id+"F2.wireOp",EDGE,"E66.0.0"),sQuery(id+"F2.wireOp",EDGE,"E66.0.1"),sQuery(id+"F2.wireOp",EDGE,"E66.0.2"),sQuery(id+"F2.wireOp",EDGE,"E66.0.3"),sQuery(id+"F2.wireOp",EDGE,"E66.0.4"),sQuery(id+"F2.wireOp",EDGE,"E66.0.5"),sQuery(id+"F2.wireOp",EDGE,"E66.0.6"),sQuery(id+"F2.wireOp",EDGE,"E66.0.7"),sQuery(id+"F2.wireOp",EDGE,"E66.0.8"),sQuery(id+"F2.wireOp",EDGE,"E66.0.9"),sQuery(id+"F2.wireOp",EDGE,"E67.0.0"),sQuery(id+"F2.wireOp",EDGE,"E67.0.1"),sQuery(id+"F2.wireOp",EDGE,"E67.0.2"),sQuery(id+"F2.wireOp",EDGE,"E67.0.3"),sQuery(id+"F2.wireOp",EDGE,"E67.0.4"),sQuery(id+"F2.wireOp",EDGE,"E67.0.5"),sQuery(id+"F2.wireOp",EDGE,"E67.0.6"),sQuery(id+"F2.wireOp",EDGE,"E67.0.7"),sQuery(id+"F2.wireOp",EDGE,"E67.0.8"),sQuery(id+"F2.wireOp",EDGE,"E67.0.9"),sQuery(id+"F2.wireOp",EDGE,"E68.0.0"),sQuery(id+"F2.wireOp",EDGE,"E68.0.1"),sQuery(id+"F2.wireOp",EDGE,"E68.0.2"),sQuery(id+"F2.wireOp",EDGE,"E68.0.3"),sQuery(id+"F2.wireOp",EDGE,"E68.0.4"),sQuery(id+"F2.wireOp",EDGE,"E68.0.5"),sQuery(id+"F2.wireOp",EDGE,"E68.0.6"),sQuery(id+"F2.wireOp",EDGE,"E68.0.7"),sQuery(id+"F2.wireOp",EDGE,"E68.0.8"),sQuery(id+"F2.wireOp",EDGE,"E68.0.9"),sQuery(id+"F2.wireOp",EDGE,"E69.0.0"),sQuery(id+"F2.wireOp",EDGE,"E69.0.1"),sQuery(id+"F2.wireOp",EDGE,"E69.0.2"),sQuery(id+"F2.wireOp",EDGE,"E69.0.3"),sQuery(id+"F2.wireOp",EDGE,"E69.0.4"),sQuery(id+"F2.wireOp",EDGE,"E69.0.5"),sQuery(id+"F2.wireOp",EDGE,"E69.0.6"),sQuery(id+"F2.wireOp",EDGE,"E69.0.7"),sQuery(id+"F2.wireOp",EDGE,"E69.0.8"),sQuery(id+"F2.wireOp",EDGE,"E69.0.9"),sQuery(id+"F2.wireOp",EDGE,"E70.0.0"),sQuery(id+"F2.wireOp",EDGE,"E70.0.1"),sQuery(id+"F2.wireOp",EDGE,"E70.0.2"),sQuery(id+"F2.wireOp",EDGE,"E70.0.3"),sQuery(id+"F2.wireOp",EDGE,"E70.0.4"),sQuery(id+"F2.wireOp",EDGE,"E70.0.5"),sQuery(id+"F2.wireOp",EDGE,"E70.0.6"),sQuery(id+"F2.wireOp",EDGE,"E70.0.7"),sQuery(id+"F2.wireOp",EDGE,"E70.0.8"),sQuery(id+"F2.wireOp",EDGE,"E70.0.9"),sQuery(id+"F2.wireOp",EDGE,"E71.0.0"),sQuery(id+"F2.wireOp",EDGE,"E71.0.1"),sQuery(id+"F2.wireOp",EDGE,"E71.0.2"),sQuery(id+"F2.wireOp",EDGE,"E71.0.3"),sQuery(id+"F2.wireOp",EDGE,"E71.0.4"),sQuery(id+"F2.wireOp",EDGE,"E71.0.5"),sQuery(id+"F2.wireOp",EDGE,"E71.0.6"),sQuery(id+"F2.wireOp",EDGE,"E71.0.7"),sQuery(id+"F2.wireOp",EDGE,"E71.0.8"),sQuery(id+"F2.wireOp",EDGE,"E71.0.9"),sQuery(id+"F2.wireOp",EDGE,"E72.0.0"),sQuery(id+"F2.wireOp",EDGE,"E72.0.1"),sQuery(id+"F2.wireOp",EDGE,"E72.0.2"),sQuery(id+"F2.wireOp",EDGE,"E72.0.3"),sQuery(id+"F2.wireOp",EDGE,"E72.0.4"),sQuery(id+"F2.wireOp",EDGE,"E72.0.5"),sQuery(id+"F2.wireOp",EDGE,"E72.0.6"),sQuery(id+"F2.wireOp",EDGE,"E72.0.7"),sQuery(id+"F2.wireOp",EDGE,"E72.0.8"),sQuery(id+"F2.wireOp",EDGE,"E72.0.9"),sQuery(id+"F2.wireOp",EDGE,"E72.0.10"),sQuery(id+"F2.wireOp",EDGE,"E72.0.11"),sQuery(id+"F2.wireOp",EDGE,"E72.0.12"),sQuery(id+"F2.wireOp",EDGE,"E72.0.13"),sQuery(id+"F2.wireOp",EDGE,"E72.0.14"),sQuery(id+"F2.wireOp",EDGE,"E72.0.15"),sQuery(id+"F2.wireOp",EDGE,"E72.0.16"),sQuery(id+"F2.wireOp",EDGE,"E72.0.17")])],"isStart":false});
            fillet(context, id + "F14", {"entities" : qUnion([Q0]), "radius" : 1 * mm, "tangentPropagation" : true, "allowEdgeOverflow" : false});
        }
        {
            var Q0;
            Q0=makeQuery(id+"F5.opExtrude","CAP_EDGE",EDGE,{"disambiguationData":[OSD([sQuery(id+"F0.wireOp",EDGE,"E57")])],"isStart":false});
            var Q1;
            Q1=makeQuery(id+"F5.opExtrude","CAP_EDGE",EDGE,{"disambiguationData":[OSD([sQuery(id+"F0.wireOp",EDGE,"E58.5.0")])],"isStart":false});
            var Q2;
            Q2=makeQuery(id+"F5.opExtrude","CAP_EDGE",EDGE,{"disambiguationData":[OSD([sQuery(id+"F0.wireOp",EDGE,"E58.4.0")])],"isStart":false});
            var Q3;
            Q3=makeQuery(id+"F5.opExtrude","CAP_EDGE",EDGE,{"disambiguationData":[OSD([sQuery(id+"F0.wireOp",EDGE,"E58.3.0")])],"isStart":false});
            var Q4;
            Q4=makeQuery(id+"F5.opExtrude","CAP_EDGE",EDGE,{"disambiguationData":[OSD([sQuery(id+"F0.wireOp",EDGE,"E58.2.0")])],"isStart":false});
            var Q5;
            Q5=makeQuery(id+"F5.opExtrude","CAP_EDGE",EDGE,{"disambiguationData":[OSD([sQuery(id+"F0.wireOp",EDGE,"E58.1.0")])],"isStart":false});
            fillet(context, id + "F15", {"entities" : qUnion([Q0, Q1, Q2, Q3, Q4, Q5]), "radius" : 1 * mm, "tangentPropagation" : true, "allowEdgeOverflow" : false});
        }
        {
            var Q0;
            Q0=makeQuery(id+"F5.opExtrude","CAP_EDGE",EDGE,{"disambiguationData":[OSD([sQuery(id+"F0.wireOp",EDGE,"E7.5.4")])],"isStart":true});
            var Q1;
            Q1=makeQuery(id+"F5.opExtrude","CAP_EDGE",EDGE,{"disambiguationData":[OSD([sQuery(id+"F0.wireOp",EDGE,"E1")])],"isStart":true});
            var Q2;
            Q2=makeQuery(id+"F5.opExtrude","CAP_EDGE",EDGE,{"disambiguationData":[OSD([sQuery(id+"F0.wireOp",EDGE,"E7.1.3")])],"isStart":true});
            var Q3;
            Q3=makeQuery(id+"F5.opExtrude","CAP_EDGE",EDGE,{"disambiguationData":[OSD([sQuery(id+"F0.wireOp",EDGE,"E10.trimOffspring")])],"isStart":true});
            var Q4;
            Q4=makeQuery(id+"F5.opExtrude","CAP_EDGE",EDGE,{"disambiguationData":[OSD([sQuery(id+"F0.wireOp",EDGE,"E12.trimOffspring")])],"isStart":true});
            var Q5;
            Q5=makeQuery(id+"F5.opExtrude","CAP_EDGE",EDGE,{"disambiguationData":[OSD([sQuery(id+"F0.wireOp",EDGE,"E17.trimOffspring")])],"isStart":true});
            fillet(context, id + "F16", {"entities" : qUnion([Q0, Q1, Q2, Q3, Q4, Q5]), "radius" : 1 * mm, "tangentPropagation" : true, "allowEdgeOverflow" : false});
        }
        {
            var Q0;
            Q0=makeQuery(id+"F5.opExtrude","CAP_EDGE",EDGE,{"disambiguationData":[OSD([sQuery(id+"F0.wireOp",EDGE,"E26.4.2")])],"isStart":true});
            fillet(context, id + "F17", {"entities" : qUnion([Q0]), "radius" : 1 * mm, "tangentPropagation" : true, "allowEdgeOverflow" : false});
        }
    });
